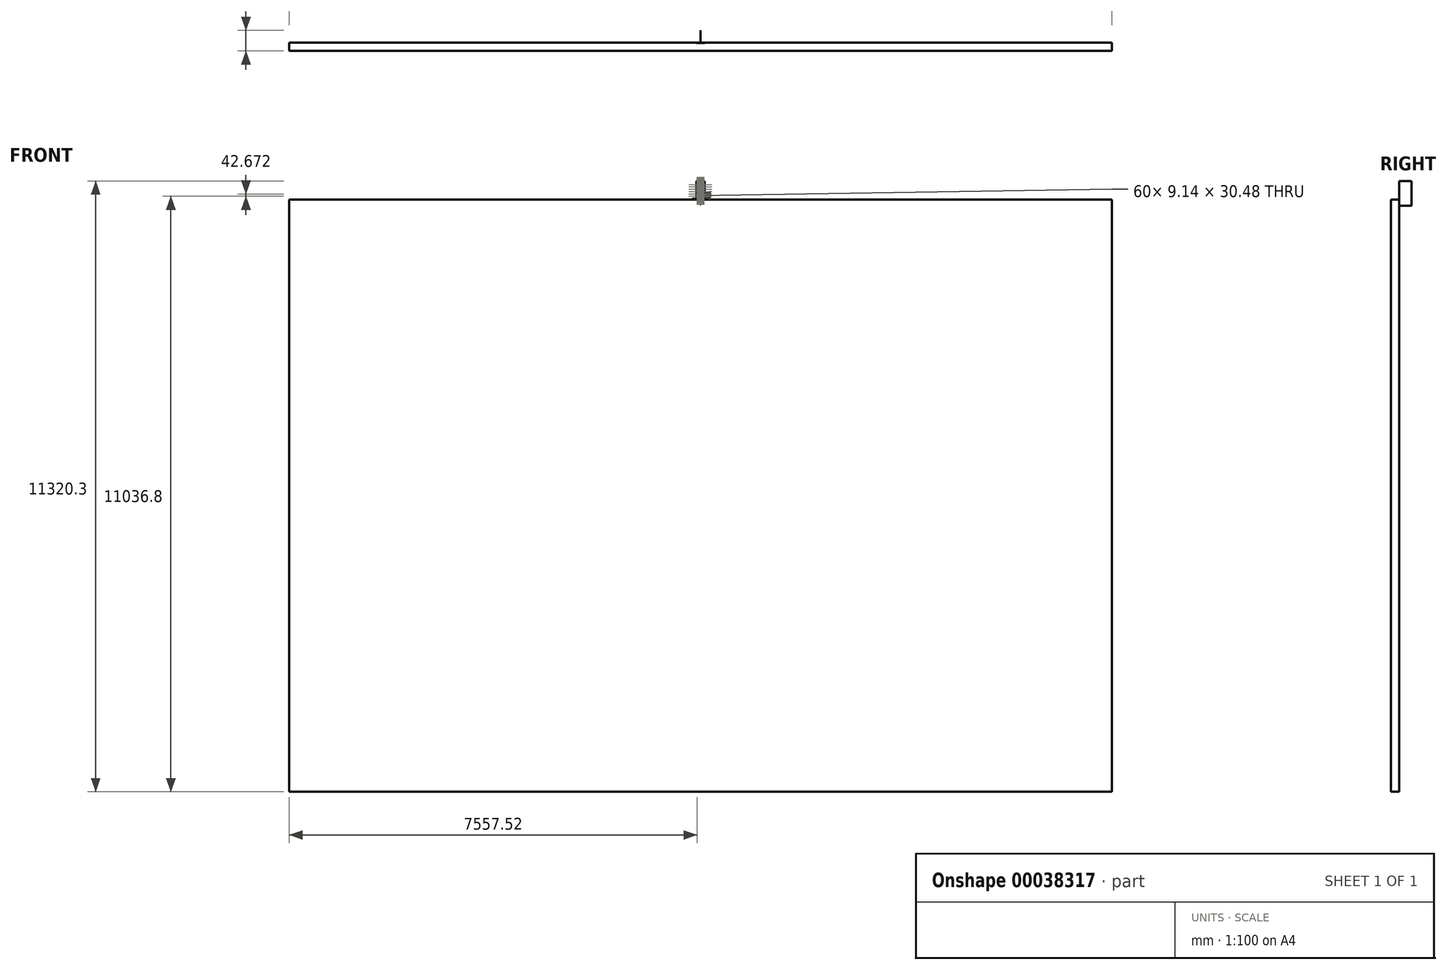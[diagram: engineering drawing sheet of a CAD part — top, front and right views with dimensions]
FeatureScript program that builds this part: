
annotation { "Feature Type Name" : "Feature", "Feature Type Description" : "" }
export const myFeature = defineFeature(function(context is Context, id is Id, definition is map)
    precondition{}
    {
        {
            var Q0;
            Q0=qCreatedBy(makeId("Front.planeOp"),FACE);
            var sketch = newSketch(context, id + "F0", { "sketchPlane" : qUnion([Q0])});
            skLineSegment(sketch, "E0", {"start": v(0, 0) * mm, "end": v(0, 37251.06) * mm, "construction": true});
            skLineSegment(sketch, "E1.bottom", {"start": v(-7620, 0) * mm, "end": v(7620, 0) * mm});
            skLineSegment(sketch, "E1.top", {"start": v(-7620, 34747.2) * mm, "end": v(7620, 34747.2) * mm});
            skLineSegment(sketch, "E1.left", {"start": v(-7620, 0) * mm, "end": v(-7620, 34747.2) * mm});
            skLineSegment(sketch, "E1.right", {"start": v(7620, 0) * mm, "end": v(7620, 34747.2) * mm});
            skLineSegment(sketch, "E2.bottom", {"start": v(-6705.6, 4876.8) * mm, "end": v(-5791.2, 4876.8) * mm});
            skLineSegment(sketch, "E2.top", {"start": v(-6705.6, 7924.8) * mm, "end": v(-5791.2, 7924.8) * mm});
            skLineSegment(sketch, "E2.left", {"start": v(-6705.6, 4876.8) * mm, "end": v(-6705.6, 7924.8) * mm});
            skLineSegment(sketch, "E2.right", {"start": v(-5791.2, 4876.8) * mm, "end": v(-5791.2, 7924.8) * mm});
            skLineSegment(sketch, "E3.0.1.0", {"start": v(-6705.6, 9144) * mm, "end": v(-6705.6, 12192) * mm});
            skLineSegment(sketch, "E3.0.1.1", {"start": v(-5791.2, 9144) * mm, "end": v(-5791.2, 12192) * mm});
            skLineSegment(sketch, "E3.0.1.2", {"start": v(-6705.6, 12192) * mm, "end": v(-5791.2, 12192) * mm});
            skLineSegment(sketch, "E3.0.1.3", {"start": v(-6705.6, 9144) * mm, "end": v(-5791.2, 9144) * mm});
            skLineSegment(sketch, "E3.0.2.0", {"start": v(-6705.6, 13411.2) * mm, "end": v(-6705.6, 16459.2) * mm});
            skLineSegment(sketch, "E3.0.2.1", {"start": v(-5791.2, 13411.2) * mm, "end": v(-5791.2, 16459.2) * mm});
            skLineSegment(sketch, "E3.0.2.2", {"start": v(-6705.6, 16459.2) * mm, "end": v(-5791.2, 16459.2) * mm});
            skLineSegment(sketch, "E3.0.2.3", {"start": v(-6705.6, 13411.2) * mm, "end": v(-5791.2, 13411.2) * mm});
            skLineSegment(sketch, "E3.0.3.0", {"start": v(-6705.6, 17678.4) * mm, "end": v(-6705.6, 20726.4) * mm});
            skLineSegment(sketch, "E3.0.3.1", {"start": v(-5791.2, 17678.4) * mm, "end": v(-5791.2, 20726.4) * mm});
            skLineSegment(sketch, "E3.0.3.2", {"start": v(-6705.6, 20726.4) * mm, "end": v(-5791.2, 20726.4) * mm});
            skLineSegment(sketch, "E3.0.3.3", {"start": v(-6705.6, 17678.4) * mm, "end": v(-5791.2, 17678.4) * mm});
            skLineSegment(sketch, "E3.0.4.0", {"start": v(-6705.6, 21945.6) * mm, "end": v(-6705.6, 24993.6) * mm});
            skLineSegment(sketch, "E3.0.4.1", {"start": v(-5791.2, 21945.6) * mm, "end": v(-5791.2, 24993.6) * mm});
            skLineSegment(sketch, "E3.0.4.2", {"start": v(-6705.6, 24993.6) * mm, "end": v(-5791.2, 24993.6) * mm});
            skLineSegment(sketch, "E3.0.4.3", {"start": v(-6705.6, 21945.6) * mm, "end": v(-5791.2, 21945.6) * mm});
            skLineSegment(sketch, "E3.0.5.0", {"start": v(-6705.6, 26212.8) * mm, "end": v(-6705.6, 29260.8) * mm});
            skLineSegment(sketch, "E3.0.5.1", {"start": v(-5791.2, 26212.8) * mm, "end": v(-5791.2, 29260.8) * mm});
            skLineSegment(sketch, "E3.0.5.2", {"start": v(-6705.6, 29260.8) * mm, "end": v(-5791.2, 29260.8) * mm});
            skLineSegment(sketch, "E3.0.5.3", {"start": v(-6705.6, 26212.8) * mm, "end": v(-5791.2, 26212.8) * mm});
            skLineSegment(sketch, "E3.1.0.0", {"start": v(-5486.4, 4876.8) * mm, "end": v(-5486.4, 7924.8) * mm});
            skLineSegment(sketch, "E3.1.0.1", {"start": v(-4572, 4876.8) * mm, "end": v(-4572, 7924.8) * mm});
            skLineSegment(sketch, "E3.1.0.2", {"start": v(-5486.4, 7924.8) * mm, "end": v(-4572, 7924.8) * mm});
            skLineSegment(sketch, "E3.1.0.3", {"start": v(-5486.4, 4876.8) * mm, "end": v(-4572, 4876.8) * mm});
            skLineSegment(sketch, "E3.1.1.0", {"start": v(-5486.4, 9144) * mm, "end": v(-5486.4, 12192) * mm});
            skLineSegment(sketch, "E3.1.1.1", {"start": v(-4572, 9144) * mm, "end": v(-4572, 12192) * mm});
            skLineSegment(sketch, "E3.1.1.2", {"start": v(-5486.4, 12192) * mm, "end": v(-4572, 12192) * mm});
            skLineSegment(sketch, "E3.1.1.3", {"start": v(-5486.4, 9144) * mm, "end": v(-4572, 9144) * mm});
            skLineSegment(sketch, "E3.1.2.0", {"start": v(-5486.4, 13411.2) * mm, "end": v(-5486.4, 16459.2) * mm});
            skLineSegment(sketch, "E3.1.2.1", {"start": v(-4572, 13411.2) * mm, "end": v(-4572, 16459.2) * mm});
            skLineSegment(sketch, "E3.1.2.2", {"start": v(-5486.4, 16459.2) * mm, "end": v(-4572, 16459.2) * mm});
            skLineSegment(sketch, "E3.1.2.3", {"start": v(-5486.4, 13411.2) * mm, "end": v(-4572, 13411.2) * mm});
            skLineSegment(sketch, "E3.1.3.0", {"start": v(-5486.4, 17678.4) * mm, "end": v(-5486.4, 20726.4) * mm});
            skLineSegment(sketch, "E3.1.3.1", {"start": v(-4572, 17678.4) * mm, "end": v(-4572, 20726.4) * mm});
            skLineSegment(sketch, "E3.1.3.2", {"start": v(-5486.4, 20726.4) * mm, "end": v(-4572, 20726.4) * mm});
            skLineSegment(sketch, "E3.1.3.3", {"start": v(-5486.4, 17678.4) * mm, "end": v(-4572, 17678.4) * mm});
            skLineSegment(sketch, "E3.1.4.0", {"start": v(-5486.4, 21945.6) * mm, "end": v(-5486.4, 24993.6) * mm});
            skLineSegment(sketch, "E3.1.4.1", {"start": v(-4572, 21945.6) * mm, "end": v(-4572, 24993.6) * mm});
            skLineSegment(sketch, "E3.1.4.2", {"start": v(-5486.4, 24993.6) * mm, "end": v(-4572, 24993.6) * mm});
            skLineSegment(sketch, "E3.1.4.3", {"start": v(-5486.4, 21945.6) * mm, "end": v(-4572, 21945.6) * mm});
            skLineSegment(sketch, "E3.1.5.0", {"start": v(-5486.4, 26212.8) * mm, "end": v(-5486.4, 29260.8) * mm});
            skLineSegment(sketch, "E3.1.5.1", {"start": v(-4572, 26212.8) * mm, "end": v(-4572, 29260.8) * mm});
            skLineSegment(sketch, "E3.1.5.2", {"start": v(-5486.4, 29260.8) * mm, "end": v(-4572, 29260.8) * mm});
            skLineSegment(sketch, "E3.1.5.3", {"start": v(-5486.4, 26212.8) * mm, "end": v(-4572, 26212.8) * mm});
            skLineSegment(sketch, "E3.2.0.0", {"start": v(-4267.2, 4876.8) * mm, "end": v(-4267.2, 7924.8) * mm});
            skLineSegment(sketch, "E3.2.0.1", {"start": v(-3352.8, 4876.8) * mm, "end": v(-3352.8, 7924.8) * mm});
            skLineSegment(sketch, "E3.2.0.2", {"start": v(-4267.2, 7924.8) * mm, "end": v(-3352.8, 7924.8) * mm});
            skLineSegment(sketch, "E3.2.0.3", {"start": v(-4267.2, 4876.8) * mm, "end": v(-3352.8, 4876.8) * mm});
            skLineSegment(sketch, "E3.2.1.0", {"start": v(-4267.2, 9144) * mm, "end": v(-4267.2, 12192) * mm});
            skLineSegment(sketch, "E3.2.1.1", {"start": v(-3352.8, 9144) * mm, "end": v(-3352.8, 12192) * mm});
            skLineSegment(sketch, "E3.2.1.2", {"start": v(-4267.2, 12192) * mm, "end": v(-3352.8, 12192) * mm});
            skLineSegment(sketch, "E3.2.1.3", {"start": v(-4267.2, 9144) * mm, "end": v(-3352.8, 9144) * mm});
            skLineSegment(sketch, "E3.2.2.0", {"start": v(-4267.2, 13411.2) * mm, "end": v(-4267.2, 16459.2) * mm});
            skLineSegment(sketch, "E3.2.2.1", {"start": v(-3352.8, 13411.2) * mm, "end": v(-3352.8, 16459.2) * mm});
            skLineSegment(sketch, "E3.2.2.2", {"start": v(-4267.2, 16459.2) * mm, "end": v(-3352.8, 16459.2) * mm});
            skLineSegment(sketch, "E3.2.2.3", {"start": v(-4267.2, 13411.2) * mm, "end": v(-3352.8, 13411.2) * mm});
            skLineSegment(sketch, "E3.2.3.0", {"start": v(-4267.2, 17678.4) * mm, "end": v(-4267.2, 20726.4) * mm});
            skLineSegment(sketch, "E3.2.3.1", {"start": v(-3352.8, 17678.4) * mm, "end": v(-3352.8, 20726.4) * mm});
            skLineSegment(sketch, "E3.2.3.2", {"start": v(-4267.2, 20726.4) * mm, "end": v(-3352.8, 20726.4) * mm});
            skLineSegment(sketch, "E3.2.3.3", {"start": v(-4267.2, 17678.4) * mm, "end": v(-3352.8, 17678.4) * mm});
            skLineSegment(sketch, "E3.2.4.0", {"start": v(-4267.2, 21945.6) * mm, "end": v(-4267.2, 24993.6) * mm});
            skLineSegment(sketch, "E3.2.4.1", {"start": v(-3352.8, 21945.6) * mm, "end": v(-3352.8, 24993.6) * mm});
            skLineSegment(sketch, "E3.2.4.2", {"start": v(-4267.2, 24993.6) * mm, "end": v(-3352.8, 24993.6) * mm});
            skLineSegment(sketch, "E3.2.4.3", {"start": v(-4267.2, 21945.6) * mm, "end": v(-3352.8, 21945.6) * mm});
            skLineSegment(sketch, "E3.2.5.0", {"start": v(-4267.2, 26212.8) * mm, "end": v(-4267.2, 29260.8) * mm});
            skLineSegment(sketch, "E3.2.5.1", {"start": v(-3352.8, 26212.8) * mm, "end": v(-3352.8, 29260.8) * mm});
            skLineSegment(sketch, "E3.2.5.2", {"start": v(-4267.2, 29260.8) * mm, "end": v(-3352.8, 29260.8) * mm});
            skLineSegment(sketch, "E3.2.5.3", {"start": v(-4267.2, 26212.8) * mm, "end": v(-3352.8, 26212.8) * mm});
            skLineSegment(sketch, "E3.direction1", {"start": v(-6705.6, 4876.8) * mm, "end": v(-5486.4, 4876.8) * mm, "construction": true});
            skLineSegment(sketch, "E3.direction2", {"start": v(-6705.6, 4876.8) * mm, "end": v(-6705.6, 9144) * mm, "construction": true});
            skLineSegment(sketch, "E4.MirrorCS", {"start": v(5486.4, 9144) * mm, "end": v(4572, 9144) * mm});
            skLineSegment(sketch, "E5.MirrorCS", {"start": v(5486.4, 7924.8) * mm, "end": v(4572, 7924.8) * mm});
            skLineSegment(sketch, "E6.MirrorCS", {"start": v(6705.6, 4876.8) * mm, "end": v(5791.2, 4876.8) * mm});
            skLineSegment(sketch, "E7.MirrorCS", {"start": v(6705.6, 7924.8) * mm, "end": v(5791.2, 7924.8) * mm});
            skLineSegment(sketch, "E8.MirrorCS", {"start": v(6705.6, 9144) * mm, "end": v(5791.2, 9144) * mm});
            skLineSegment(sketch, "E9.MirrorCS", {"start": v(4267.2, 20726.4) * mm, "end": v(3352.8, 20726.4) * mm});
            skLineSegment(sketch, "E10.MirrorCS", {"start": v(5486.4, 29260.8) * mm, "end": v(4572, 29260.8) * mm});
            skLineSegment(sketch, "E11.MirrorCS", {"start": v(5486.4, 12192) * mm, "end": v(4572, 12192) * mm});
            skLineSegment(sketch, "E12.MirrorCS", {"start": v(4267.2, 12192) * mm, "end": v(3352.8, 12192) * mm});
            skLineSegment(sketch, "E13.MirrorCS", {"start": v(5486.4, 20726.4) * mm, "end": v(4572, 20726.4) * mm});
            skLineSegment(sketch, "E14.MirrorCS", {"start": v(4267.2, 29260.8) * mm, "end": v(3352.8, 29260.8) * mm});
            skLineSegment(sketch, "E15.MirrorCS", {"start": v(6705.6, 17678.4) * mm, "end": v(5791.2, 17678.4) * mm});
            skLineSegment(sketch, "E16.MirrorCS", {"start": v(4267.2, 17678.4) * mm, "end": v(3352.8, 17678.4) * mm});
            skLineSegment(sketch, "E17.MirrorCS", {"start": v(5486.4, 26212.8) * mm, "end": v(4572, 26212.8) * mm});
            skLineSegment(sketch, "E18.MirrorCS", {"start": v(4267.2, 9144) * mm, "end": v(3352.8, 9144) * mm});
            skLineSegment(sketch, "E19.MirrorCS", {"start": v(5486.4, 17678.4) * mm, "end": v(4572, 17678.4) * mm});
            skLineSegment(sketch, "E20.MirrorCS", {"start": v(6705.6, 26212.8) * mm, "end": v(5791.2, 26212.8) * mm});
            skLineSegment(sketch, "E21.MirrorCS", {"start": v(4267.2, 26212.8) * mm, "end": v(3352.8, 26212.8) * mm});
            skLineSegment(sketch, "E22.MirrorCS", {"start": v(4267.2, 16459.2) * mm, "end": v(3352.8, 16459.2) * mm});
            skLineSegment(sketch, "E23.MirrorCS", {"start": v(5486.4, 24993.6) * mm, "end": v(4572, 24993.6) * mm});
            skLineSegment(sketch, "E24.MirrorCS", {"start": v(6705.6, 16459.2) * mm, "end": v(5791.2, 16459.2) * mm});
            skLineSegment(sketch, "E25.MirrorCS", {"start": v(4267.2, 7924.8) * mm, "end": v(3352.8, 7924.8) * mm});
            skLineSegment(sketch, "E26.MirrorCS", {"start": v(5486.4, 16459.2) * mm, "end": v(4572, 16459.2) * mm});
            skLineSegment(sketch, "E27.MirrorCS", {"start": v(6705.6, 24993.6) * mm, "end": v(5791.2, 24993.6) * mm});
            skLineSegment(sketch, "E28.MirrorCS", {"start": v(4267.2, 24993.6) * mm, "end": v(3352.8, 24993.6) * mm});
            skLineSegment(sketch, "E29.MirrorCS", {"start": v(4267.2, 13411.2) * mm, "end": v(3352.8, 13411.2) * mm});
            skLineSegment(sketch, "E30.MirrorCS", {"start": v(5486.4, 21945.6) * mm, "end": v(4572, 21945.6) * mm});
            skLineSegment(sketch, "E31.MirrorCS", {"start": v(5486.4, 4876.8) * mm, "end": v(4572, 4876.8) * mm});
            skLineSegment(sketch, "E32.MirrorCS", {"start": v(4267.2, 4876.8) * mm, "end": v(3352.8, 4876.8) * mm});
            skLineSegment(sketch, "E33.MirrorCS", {"start": v(5486.4, 13411.2) * mm, "end": v(4572, 13411.2) * mm});
            skLineSegment(sketch, "E34.MirrorCS", {"start": v(4267.2, 21945.6) * mm, "end": v(3352.8, 21945.6) * mm});
            skLineSegment(sketch, "E35.MirrorCS", {"start": v(6705.6, 20726.4) * mm, "end": v(5791.2, 20726.4) * mm});
            skLineSegment(sketch, "E36.MirrorCS", {"start": v(6705.6, 29260.8) * mm, "end": v(5791.2, 29260.8) * mm});
            skLineSegment(sketch, "E37.MirrorCS", {"start": v(6705.6, 12192) * mm, "end": v(5791.2, 12192) * mm});
            skLineSegment(sketch, "E38.MirrorCS", {"start": v(6705.6, 13411.2) * mm, "end": v(5791.2, 13411.2) * mm});
            skLineSegment(sketch, "E39.MirrorCS", {"start": v(6705.6, 21945.6) * mm, "end": v(5791.2, 21945.6) * mm});
            skLineSegment(sketch, "E40.MirrorCS", {"start": v(3352.8, 9144) * mm, "end": v(3352.8, 12192) * mm});
            skLineSegment(sketch, "E41.MirrorCS", {"start": v(4572, 17678.4) * mm, "end": v(4572, 20726.4) * mm});
            skLineSegment(sketch, "E42.MirrorCS", {"start": v(3352.8, 26212.8) * mm, "end": v(3352.8, 29260.8) * mm});
            skLineSegment(sketch, "E43.MirrorCS", {"start": v(5791.2, 26212.8) * mm, "end": v(5791.2, 29260.8) * mm});
            skLineSegment(sketch, "E44.MirrorCS", {"start": v(4267.2, 13411.2) * mm, "end": v(4267.2, 16459.2) * mm});
            skLineSegment(sketch, "E45.MirrorCS", {"start": v(5486.4, 21945.6) * mm, "end": v(5486.4, 24993.6) * mm});
            skLineSegment(sketch, "E46.MirrorCS", {"start": v(5486.4, 4876.8) * mm, "end": v(5486.4, 7924.8) * mm});
            skLineSegment(sketch, "E47.MirrorCS", {"start": v(6705.6, 21945.6) * mm, "end": v(6705.6, 24993.6) * mm});
            skLineSegment(sketch, "E48.MirrorCS", {"start": v(3352.8, 13411.2) * mm, "end": v(3352.8, 16459.2) * mm});
            skLineSegment(sketch, "E49.MirrorCS", {"start": v(4267.2, 21945.6) * mm, "end": v(4267.2, 24993.6) * mm});
            skLineSegment(sketch, "E50.MirrorCS", {"start": v(4267.2, 4876.8) * mm, "end": v(4267.2, 7924.8) * mm});
            skLineSegment(sketch, "E51.MirrorCS", {"start": v(4572, 21945.6) * mm, "end": v(4572, 24993.6) * mm});
            skLineSegment(sketch, "E52.MirrorCS", {"start": v(5486.4, 13411.2) * mm, "end": v(5486.4, 16459.2) * mm});
            skLineSegment(sketch, "E53.MirrorCS", {"start": v(4572, 4876.8) * mm, "end": v(4572, 7924.8) * mm});
            skLineSegment(sketch, "E54.MirrorCS", {"start": v(5791.2, 21945.6) * mm, "end": v(5791.2, 24993.6) * mm});
            skLineSegment(sketch, "E55.MirrorCS", {"start": v(3352.8, 21945.6) * mm, "end": v(3352.8, 24993.6) * mm});
            skLineSegment(sketch, "E56.MirrorCS", {"start": v(3352.8, 4876.8) * mm, "end": v(3352.8, 7924.8) * mm});
            skLineSegment(sketch, "E57.MirrorCS", {"start": v(4572, 13411.2) * mm, "end": v(4572, 16459.2) * mm});
            skLineSegment(sketch, "E58.MirrorCS", {"start": v(6705.6, 13411.2) * mm, "end": v(6705.6, 16459.2) * mm});
            skLineSegment(sketch, "E59.MirrorCS", {"start": v(5791.2, 13411.2) * mm, "end": v(5791.2, 16459.2) * mm});
            skLineSegment(sketch, "E60.MirrorCS", {"start": v(6705.6, 4876.8) * mm, "end": v(6705.6, 7924.8) * mm});
            skLineSegment(sketch, "E61.MirrorCS", {"start": v(5791.2, 4876.8) * mm, "end": v(5791.2, 7924.8) * mm});
            skLineSegment(sketch, "E62.MirrorCS", {"start": v(6705.6, 9144) * mm, "end": v(6705.6, 12192) * mm});
            skLineSegment(sketch, "E63.MirrorCS", {"start": v(5791.2, 9144) * mm, "end": v(5791.2, 12192) * mm});
            skLineSegment(sketch, "E64.MirrorCS", {"start": v(6705.6, 17678.4) * mm, "end": v(6705.6, 20726.4) * mm});
            skLineSegment(sketch, "E65.MirrorCS", {"start": v(4267.2, 17678.4) * mm, "end": v(4267.2, 20726.4) * mm});
            skLineSegment(sketch, "E66.MirrorCS", {"start": v(5486.4, 26212.8) * mm, "end": v(5486.4, 29260.8) * mm});
            skLineSegment(sketch, "E67.MirrorCS", {"start": v(5486.4, 9144) * mm, "end": v(5486.4, 12192) * mm});
            skLineSegment(sketch, "E68.MirrorCS", {"start": v(4267.2, 9144) * mm, "end": v(4267.2, 12192) * mm});
            skLineSegment(sketch, "E69.MirrorCS", {"start": v(5486.4, 17678.4) * mm, "end": v(5486.4, 20726.4) * mm});
            skLineSegment(sketch, "E70.MirrorCS", {"start": v(4267.2, 26212.8) * mm, "end": v(4267.2, 29260.8) * mm});
            skLineSegment(sketch, "E71.MirrorCS", {"start": v(6705.6, 26212.8) * mm, "end": v(6705.6, 29260.8) * mm});
            skLineSegment(sketch, "E72.MirrorCS", {"start": v(4572, 9144) * mm, "end": v(4572, 12192) * mm});
            skLineSegment(sketch, "E73.MirrorCS", {"start": v(4572, 26212.8) * mm, "end": v(4572, 29260.8) * mm});
            skLineSegment(sketch, "E74.MirrorCS", {"start": v(3352.8, 17678.4) * mm, "end": v(3352.8, 20726.4) * mm});
            skLineSegment(sketch, "E75.MirrorCS", {"start": v(5791.2, 17678.4) * mm, "end": v(5791.2, 20726.4) * mm});
            skLineSegment(sketch, "E76.bottom", {"start": v(6705.6, 31089.6) * mm, "end": v(5791.2, 31089.6) * mm});
            skLineSegment(sketch, "E76.top", {"start": v(6705.6, 32918.4) * mm, "end": v(5791.2, 32918.4) * mm});
            skLineSegment(sketch, "E76.left", {"start": v(6705.6, 31089.6) * mm, "end": v(6705.6, 32918.4) * mm});
            skLineSegment(sketch, "E76.right", {"start": v(5791.2, 31089.6) * mm, "end": v(5791.2, 32918.4) * mm});
            skLineSegment(sketch, "E77.bottom", {"start": v(5486.4, 31089.6) * mm, "end": v(4572, 31089.6) * mm});
            skLineSegment(sketch, "E77.top", {"start": v(5486.4, 32918.4) * mm, "end": v(4572, 32918.4) * mm});
            skLineSegment(sketch, "E77.left", {"start": v(5486.4, 31089.6) * mm, "end": v(5486.4, 32918.4) * mm});
            skLineSegment(sketch, "E77.right", {"start": v(4572, 31089.6) * mm, "end": v(4572, 32918.4) * mm});
            skLineSegment(sketch, "E78.bottom", {"start": v(4267.2, 31089.6) * mm, "end": v(3352.8, 31089.6) * mm});
            skLineSegment(sketch, "E78.top", {"start": v(4267.2, 32918.4) * mm, "end": v(3352.8, 32918.4) * mm});
            skLineSegment(sketch, "E78.left", {"start": v(4267.2, 31089.6) * mm, "end": v(4267.2, 32918.4) * mm});
            skLineSegment(sketch, "E78.right", {"start": v(3352.8, 31089.6) * mm, "end": v(3352.8, 32918.4) * mm});
            skLineSegment(sketch, "E79.bottom", {"start": v(-6705.6, 31089.6) * mm, "end": v(-5791.2, 31089.6) * mm});
            skLineSegment(sketch, "E79.top", {"start": v(-6705.6, 32918.4) * mm, "end": v(-5791.2, 32918.4) * mm});
            skLineSegment(sketch, "E79.left", {"start": v(-6705.6, 31089.6) * mm, "end": v(-6705.6, 32918.4) * mm});
            skLineSegment(sketch, "E79.right", {"start": v(-5791.2, 31089.6) * mm, "end": v(-5791.2, 32918.4) * mm});
            skLineSegment(sketch, "E80.bottom", {"start": v(-5486.4, 31089.6) * mm, "end": v(-4572, 31089.6) * mm});
            skLineSegment(sketch, "E80.top", {"start": v(-5486.4, 32918.4) * mm, "end": v(-4572, 32918.4) * mm});
            skLineSegment(sketch, "E80.left", {"start": v(-5486.4, 31089.6) * mm, "end": v(-5486.4, 32918.4) * mm});
            skLineSegment(sketch, "E80.right", {"start": v(-4572, 31089.6) * mm, "end": v(-4572, 32918.4) * mm});
            skLineSegment(sketch, "E81.bottom", {"start": v(-4267.2, 31089.6) * mm, "end": v(-3352.8, 31089.6) * mm});
            skLineSegment(sketch, "E81.top", {"start": v(-4267.2, 32918.4) * mm, "end": v(-3352.8, 32918.4) * mm});
            skLineSegment(sketch, "E81.left", {"start": v(-4267.2, 31089.6) * mm, "end": v(-4267.2, 32918.4) * mm});
            skLineSegment(sketch, "E81.right", {"start": v(-3352.8, 31089.6) * mm, "end": v(-3352.8, 32918.4) * mm});
            skLineSegment(sketch, "E82.bottom", {"start": v(-2286, 4876.8) * mm, "end": v(-1371.6, 4876.8) * mm});
            skLineSegment(sketch, "E82.top", {"start": v(-2286, 7924.8) * mm, "end": v(-1371.6, 7924.8) * mm});
            skLineSegment(sketch, "E82.left", {"start": v(-2286, 4876.8) * mm, "end": v(-2286, 7924.8) * mm});
            skLineSegment(sketch, "E82.right", {"start": v(-1371.6, 4876.8) * mm, "end": v(-1371.6, 7924.8) * mm});
            skLineSegment(sketch, "E83.0.1.0", {"start": v(-2286, 12192) * mm, "end": v(-1371.6, 12192) * mm});
            skLineSegment(sketch, "E83.0.1.1", {"start": v(-1371.6, 9144) * mm, "end": v(-1371.6, 12192) * mm});
            skLineSegment(sketch, "E83.0.1.2", {"start": v(-2286, 9144) * mm, "end": v(-1371.6, 9144) * mm});
            skLineSegment(sketch, "E83.0.1.3", {"start": v(-2286, 9144) * mm, "end": v(-2286, 12192) * mm});
            skLineSegment(sketch, "E83.0.2.0", {"start": v(-2286, 16459.2) * mm, "end": v(-1371.6, 16459.2) * mm});
            skLineSegment(sketch, "E83.0.2.1", {"start": v(-1371.6, 13411.2) * mm, "end": v(-1371.6, 16459.2) * mm});
            skLineSegment(sketch, "E83.0.2.2", {"start": v(-2286, 13411.2) * mm, "end": v(-1371.6, 13411.2) * mm});
            skLineSegment(sketch, "E83.0.2.3", {"start": v(-2286, 13411.2) * mm, "end": v(-2286, 16459.2) * mm});
            skLineSegment(sketch, "E83.0.3.0", {"start": v(-2286, 20726.4) * mm, "end": v(-1371.6, 20726.4) * mm});
            skLineSegment(sketch, "E83.0.3.1", {"start": v(-1371.6, 17678.4) * mm, "end": v(-1371.6, 20726.4) * mm});
            skLineSegment(sketch, "E83.0.3.2", {"start": v(-2286, 17678.4) * mm, "end": v(-1371.6, 17678.4) * mm});
            skLineSegment(sketch, "E83.0.3.3", {"start": v(-2286, 17678.4) * mm, "end": v(-2286, 20726.4) * mm});
            skLineSegment(sketch, "E83.0.4.0", {"start": v(-2286, 24993.6) * mm, "end": v(-1371.6, 24993.6) * mm});
            skLineSegment(sketch, "E83.0.4.1", {"start": v(-1371.6, 21945.6) * mm, "end": v(-1371.6, 24993.6) * mm});
            skLineSegment(sketch, "E83.0.4.2", {"start": v(-2286, 21945.6) * mm, "end": v(-1371.6, 21945.6) * mm});
            skLineSegment(sketch, "E83.0.4.3", {"start": v(-2286, 21945.6) * mm, "end": v(-2286, 24993.6) * mm});
            skLineSegment(sketch, "E83.0.5.0", {"start": v(-2286, 29260.8) * mm, "end": v(-1371.6, 29260.8) * mm});
            skLineSegment(sketch, "E83.0.5.1", {"start": v(-1371.6, 26212.8) * mm, "end": v(-1371.6, 29260.8) * mm});
            skLineSegment(sketch, "E83.0.5.2", {"start": v(-2286, 26212.8) * mm, "end": v(-1371.6, 26212.8) * mm});
            skLineSegment(sketch, "E83.0.5.3", {"start": v(-2286, 26212.8) * mm, "end": v(-2286, 29260.8) * mm});
            skLineSegment(sketch, "E83.1.0.0", {"start": v(-1066.8, 7924.8) * mm, "end": v(-152.4, 7924.8) * mm});
            skLineSegment(sketch, "E83.1.0.1", {"start": v(-152.4, 4876.8) * mm, "end": v(-152.4, 7924.8) * mm});
            skLineSegment(sketch, "E83.1.0.2", {"start": v(-1066.8, 4876.8) * mm, "end": v(-152.4, 4876.8) * mm});
            skLineSegment(sketch, "E83.1.0.3", {"start": v(-1066.8, 4876.8) * mm, "end": v(-1066.8, 7924.8) * mm});
            skLineSegment(sketch, "E83.1.1.0", {"start": v(-1066.8, 12192) * mm, "end": v(-152.4, 12192) * mm});
            skLineSegment(sketch, "E83.1.1.1", {"start": v(-152.4, 9144) * mm, "end": v(-152.4, 12192) * mm});
            skLineSegment(sketch, "E83.1.1.2", {"start": v(-1066.8, 9144) * mm, "end": v(-152.4, 9144) * mm});
            skLineSegment(sketch, "E83.1.1.3", {"start": v(-1066.8, 9144) * mm, "end": v(-1066.8, 12192) * mm});
            skLineSegment(sketch, "E83.1.2.0", {"start": v(-1066.8, 16459.2) * mm, "end": v(-152.4, 16459.2) * mm});
            skLineSegment(sketch, "E83.1.2.1", {"start": v(-152.4, 13411.2) * mm, "end": v(-152.4, 16459.2) * mm});
            skLineSegment(sketch, "E83.1.2.2", {"start": v(-1066.8, 13411.2) * mm, "end": v(-152.4, 13411.2) * mm});
            skLineSegment(sketch, "E83.1.2.3", {"start": v(-1066.8, 13411.2) * mm, "end": v(-1066.8, 16459.2) * mm});
            skLineSegment(sketch, "E83.1.3.0", {"start": v(-1066.8, 20726.4) * mm, "end": v(-152.4, 20726.4) * mm});
            skLineSegment(sketch, "E83.1.3.1", {"start": v(-152.4, 17678.4) * mm, "end": v(-152.4, 20726.4) * mm});
            skLineSegment(sketch, "E83.1.3.2", {"start": v(-1066.8, 17678.4) * mm, "end": v(-152.4, 17678.4) * mm});
            skLineSegment(sketch, "E83.1.3.3", {"start": v(-1066.8, 17678.4) * mm, "end": v(-1066.8, 20726.4) * mm});
            skLineSegment(sketch, "E83.1.4.0", {"start": v(-1066.8, 24993.6) * mm, "end": v(-152.4, 24993.6) * mm});
            skLineSegment(sketch, "E83.1.4.1", {"start": v(-152.4, 21945.6) * mm, "end": v(-152.4, 24993.6) * mm});
            skLineSegment(sketch, "E83.1.4.2", {"start": v(-1066.8, 21945.6) * mm, "end": v(-152.4, 21945.6) * mm});
            skLineSegment(sketch, "E83.1.4.3", {"start": v(-1066.8, 21945.6) * mm, "end": v(-1066.8, 24993.6) * mm});
            skLineSegment(sketch, "E83.1.5.0", {"start": v(-1066.8, 29260.8) * mm, "end": v(-152.4, 29260.8) * mm});
            skLineSegment(sketch, "E83.1.5.1", {"start": v(-152.4, 26212.8) * mm, "end": v(-152.4, 29260.8) * mm});
            skLineSegment(sketch, "E83.1.5.2", {"start": v(-1066.8, 26212.8) * mm, "end": v(-152.4, 26212.8) * mm});
            skLineSegment(sketch, "E83.1.5.3", {"start": v(-1066.8, 26212.8) * mm, "end": v(-1066.8, 29260.8) * mm});
            skLineSegment(sketch, "E83.2.0.0", {"start": v(152.4, 7924.8) * mm, "end": v(1066.8, 7924.8) * mm});
            skLineSegment(sketch, "E83.2.0.1", {"start": v(1066.8, 4876.8) * mm, "end": v(1066.8, 7924.8) * mm});
            skLineSegment(sketch, "E83.2.0.2", {"start": v(152.4, 4876.8) * mm, "end": v(1066.8, 4876.8) * mm});
            skLineSegment(sketch, "E83.2.0.3", {"start": v(152.4, 4876.8) * mm, "end": v(152.4, 7924.8) * mm});
            skLineSegment(sketch, "E83.2.1.0", {"start": v(152.4, 12192) * mm, "end": v(1066.8, 12192) * mm});
            skLineSegment(sketch, "E83.2.1.1", {"start": v(1066.8, 9144) * mm, "end": v(1066.8, 12192) * mm});
            skLineSegment(sketch, "E83.2.1.2", {"start": v(152.4, 9144) * mm, "end": v(1066.8, 9144) * mm});
            skLineSegment(sketch, "E83.2.1.3", {"start": v(152.4, 9144) * mm, "end": v(152.4, 12192) * mm});
            skLineSegment(sketch, "E83.2.2.0", {"start": v(152.4, 16459.2) * mm, "end": v(1066.8, 16459.2) * mm});
            skLineSegment(sketch, "E83.2.2.1", {"start": v(1066.8, 13411.2) * mm, "end": v(1066.8, 16459.2) * mm});
            skLineSegment(sketch, "E83.2.2.2", {"start": v(152.4, 13411.2) * mm, "end": v(1066.8, 13411.2) * mm});
            skLineSegment(sketch, "E83.2.2.3", {"start": v(152.4, 13411.2) * mm, "end": v(152.4, 16459.2) * mm});
            skLineSegment(sketch, "E83.2.3.0", {"start": v(152.4, 20726.4) * mm, "end": v(1066.8, 20726.4) * mm});
            skLineSegment(sketch, "E83.2.3.1", {"start": v(1066.8, 17678.4) * mm, "end": v(1066.8, 20726.4) * mm});
            skLineSegment(sketch, "E83.2.3.2", {"start": v(152.4, 17678.4) * mm, "end": v(1066.8, 17678.4) * mm});
            skLineSegment(sketch, "E83.2.3.3", {"start": v(152.4, 17678.4) * mm, "end": v(152.4, 20726.4) * mm});
            skLineSegment(sketch, "E83.2.4.0", {"start": v(152.4, 24993.6) * mm, "end": v(1066.8, 24993.6) * mm});
            skLineSegment(sketch, "E83.2.4.1", {"start": v(1066.8, 21945.6) * mm, "end": v(1066.8, 24993.6) * mm});
            skLineSegment(sketch, "E83.2.4.2", {"start": v(152.4, 21945.6) * mm, "end": v(1066.8, 21945.6) * mm});
            skLineSegment(sketch, "E83.2.4.3", {"start": v(152.4, 21945.6) * mm, "end": v(152.4, 24993.6) * mm});
            skLineSegment(sketch, "E83.2.5.0", {"start": v(152.4, 29260.8) * mm, "end": v(1066.8, 29260.8) * mm});
            skLineSegment(sketch, "E83.2.5.1", {"start": v(1066.8, 26212.8) * mm, "end": v(1066.8, 29260.8) * mm});
            skLineSegment(sketch, "E83.2.5.2", {"start": v(152.4, 26212.8) * mm, "end": v(1066.8, 26212.8) * mm});
            skLineSegment(sketch, "E83.2.5.3", {"start": v(152.4, 26212.8) * mm, "end": v(152.4, 29260.8) * mm});
            skLineSegment(sketch, "E83.3.0.0", {"start": v(1371.6, 7924.8) * mm, "end": v(2286, 7924.8) * mm});
            skLineSegment(sketch, "E83.3.0.1", {"start": v(2286, 4876.8) * mm, "end": v(2286, 7924.8) * mm});
            skLineSegment(sketch, "E83.3.0.2", {"start": v(1371.6, 4876.8) * mm, "end": v(2286, 4876.8) * mm});
            skLineSegment(sketch, "E83.3.0.3", {"start": v(1371.6, 4876.8) * mm, "end": v(1371.6, 7924.8) * mm});
            skLineSegment(sketch, "E83.3.1.0", {"start": v(1371.6, 12192) * mm, "end": v(2286, 12192) * mm});
            skLineSegment(sketch, "E83.3.1.1", {"start": v(2286, 9144) * mm, "end": v(2286, 12192) * mm});
            skLineSegment(sketch, "E83.3.1.2", {"start": v(1371.6, 9144) * mm, "end": v(2286, 9144) * mm});
            skLineSegment(sketch, "E83.3.1.3", {"start": v(1371.6, 9144) * mm, "end": v(1371.6, 12192) * mm});
            skLineSegment(sketch, "E83.3.2.0", {"start": v(1371.6, 16459.2) * mm, "end": v(2286, 16459.2) * mm});
            skLineSegment(sketch, "E83.3.2.1", {"start": v(2286, 13411.2) * mm, "end": v(2286, 16459.2) * mm});
            skLineSegment(sketch, "E83.3.2.2", {"start": v(1371.6, 13411.2) * mm, "end": v(2286, 13411.2) * mm});
            skLineSegment(sketch, "E83.3.2.3", {"start": v(1371.6, 13411.2) * mm, "end": v(1371.6, 16459.2) * mm});
            skLineSegment(sketch, "E83.3.3.0", {"start": v(1371.6, 20726.4) * mm, "end": v(2286, 20726.4) * mm});
            skLineSegment(sketch, "E83.3.3.1", {"start": v(2286, 17678.4) * mm, "end": v(2286, 20726.4) * mm});
            skLineSegment(sketch, "E83.3.3.2", {"start": v(1371.6, 17678.4) * mm, "end": v(2286, 17678.4) * mm});
            skLineSegment(sketch, "E83.3.3.3", {"start": v(1371.6, 17678.4) * mm, "end": v(1371.6, 20726.4) * mm});
            skLineSegment(sketch, "E83.3.4.0", {"start": v(1371.6, 24993.6) * mm, "end": v(2286, 24993.6) * mm});
            skLineSegment(sketch, "E83.3.4.1", {"start": v(2286, 21945.6) * mm, "end": v(2286, 24993.6) * mm});
            skLineSegment(sketch, "E83.3.4.2", {"start": v(1371.6, 21945.6) * mm, "end": v(2286, 21945.6) * mm});
            skLineSegment(sketch, "E83.3.4.3", {"start": v(1371.6, 21945.6) * mm, "end": v(1371.6, 24993.6) * mm});
            skLineSegment(sketch, "E83.3.5.0", {"start": v(1371.6, 29260.8) * mm, "end": v(2286, 29260.8) * mm});
            skLineSegment(sketch, "E83.3.5.1", {"start": v(2286, 26212.8) * mm, "end": v(2286, 29260.8) * mm});
            skLineSegment(sketch, "E83.3.5.2", {"start": v(1371.6, 26212.8) * mm, "end": v(2286, 26212.8) * mm});
            skLineSegment(sketch, "E83.3.5.3", {"start": v(1371.6, 26212.8) * mm, "end": v(1371.6, 29260.8) * mm});
            skLineSegment(sketch, "E83.direction1", {"start": v(-2286, 7924.8) * mm, "end": v(-1066.8, 7924.8) * mm, "construction": true});
            skLineSegment(sketch, "E83.direction2", {"start": v(-2286, 7924.8) * mm, "end": v(-2286, 12192) * mm, "construction": true});
            skLineSegment(sketch, "E84.bottom", {"start": v(-2286, 31089.6) * mm, "end": v(-1371.6, 31089.6) * mm});
            skLineSegment(sketch, "E84.top", {"start": v(-2286, 32918.4) * mm, "end": v(-1371.6, 32918.4) * mm});
            skLineSegment(sketch, "E84.left", {"start": v(-2286, 31089.6) * mm, "end": v(-2286, 32918.4) * mm});
            skLineSegment(sketch, "E84.right", {"start": v(-1371.6, 31089.6) * mm, "end": v(-1371.6, 32918.4) * mm});
            skLineSegment(sketch, "E85.bottom", {"start": v(-1066.8, 31089.6) * mm, "end": v(-152.4, 31089.6) * mm});
            skLineSegment(sketch, "E85.top", {"start": v(-1066.8, 32918.4) * mm, "end": v(-152.4, 32918.4) * mm});
            skLineSegment(sketch, "E85.left", {"start": v(-1066.8, 31089.6) * mm, "end": v(-1066.8, 32918.4) * mm});
            skLineSegment(sketch, "E85.right", {"start": v(-152.4, 31089.6) * mm, "end": v(-152.4, 32918.4) * mm});
            skLineSegment(sketch, "E86.bottom", {"start": v(152.4, 31089.6) * mm, "end": v(1066.8, 31089.6) * mm});
            skLineSegment(sketch, "E86.top", {"start": v(152.4, 32918.4) * mm, "end": v(1066.8, 32918.4) * mm});
            skLineSegment(sketch, "E86.left", {"start": v(152.4, 31089.6) * mm, "end": v(152.4, 32918.4) * mm});
            skLineSegment(sketch, "E86.right", {"start": v(1066.8, 31089.6) * mm, "end": v(1066.8, 32918.4) * mm});
            skLineSegment(sketch, "E87.bottom", {"start": v(1371.6, 31089.6) * mm, "end": v(2286, 31089.6) * mm});
            skLineSegment(sketch, "E87.top", {"start": v(1371.6, 32918.4) * mm, "end": v(2286, 32918.4) * mm});
            skLineSegment(sketch, "E87.left", {"start": v(1371.6, 31089.6) * mm, "end": v(1371.6, 32918.4) * mm});
            skLineSegment(sketch, "E87.right", {"start": v(2286, 31089.6) * mm, "end": v(2286, 32918.4) * mm});
            skLineSegment(sketch, "E88.bottom", {"start": v(-2286, 3657.6) * mm, "end": v(2286, 3657.6) * mm});
            skLineSegment(sketch, "E88.top", {"start": v(-2286, 0) * mm, "end": v(2286, 0) * mm});
            skLineSegment(sketch, "E88.left", {"start": v(-2286, 3657.6) * mm, "end": v(-2286, 0) * mm});
            skLineSegment(sketch, "E88.right", {"start": v(2286, 3657.6) * mm, "end": v(2286, 0) * mm});
            skLineSegment(sketch, "E89.bottom", {"start": v(3200.4, 3657.6) * mm, "end": v(6705.6, 3657.6) * mm});
            skLineSegment(sketch, "E89.top", {"start": v(3200.4, 0) * mm, "end": v(6705.6, 0) * mm});
            skLineSegment(sketch, "E89.left", {"start": v(3200.4, 3657.6) * mm, "end": v(3200.4, 0) * mm});
            skLineSegment(sketch, "E89.right", {"start": v(6705.6, 3657.6) * mm, "end": v(6705.6, 0) * mm});
            skLineSegment(sketch, "E90.MirrorCS", {"start": v(-3200.4, 0) * mm, "end": v(-6705.6, 0) * mm});
            skLineSegment(sketch, "E91.MirrorCS", {"start": v(-3200.4, 3657.6) * mm, "end": v(-6705.6, 3657.6) * mm});
            skLineSegment(sketch, "E92.MirrorCS", {"start": v(-6705.6, 3657.6) * mm, "end": v(-6705.6, 0) * mm});
            skLineSegment(sketch, "E93.MirrorCS", {"start": v(-3200.4, 3657.6) * mm, "end": v(-3200.4, 0) * mm});
            skSolve(sketch);
        }
        {
            var Q0;
            Q0=qCreatedBy(makeId("Front.planeOp"),FACE);
            var sketch = newSketch(context, id + "F1", { "sketchPlane" : qUnion([Q0])});
            skLineSegment(sketch, "E94.bottom", {"start": v(-7620, 0) * mm, "end": v(7620, 0) * mm});
            skLineSegment(sketch, "E94.top", {"start": v(-7620, -10972.8) * mm, "end": v(7620, -10972.8) * mm});
            skLineSegment(sketch, "E94.left", {"start": v(-7620, 0) * mm, "end": v(-7620, -10972.8) * mm});
            skLineSegment(sketch, "E94.right", {"start": v(7620, 0) * mm, "end": v(7620, -10972.8) * mm});
            skSolve(sketch);
        }
        {
            var Q0;
            Q0=makeQuery(id+"F0.imprint","IMPRINT",FACE,{"disambiguationData":[TD([[makeQuery(id+"F0.imprint","IMPRINT",EDGE,{"derivedFrom":sQuery(id+"F0.wireOp",EDGE,"E1.top")}),-1.0]])]});
            var Q1;
            Q1=makeQuery(id+"F1.imprint","IMPRINT",FACE,{"disambiguationData":[TD([[makeQuery(id+"F1.imprint","IMPRINT",EDGE,{"derivedFrom":sQuery(id+"F1.wireOp",EDGE,"E94.bottom")}),-1.0]])]});
            extrude(context, id + "F2", {"entities" : qUnion([Q0, Q1]), "depth" : 152.4 * mm});
        }
        {
            var Q0;
            Q0=qCreatedBy(makeId("Right.planeOp"),FACE);
            var sketch = newSketch(context, id + "F3", { "sketchPlane" : qUnion([Q0])});
            skLineSegment(sketch, "E95.bottom", {"start": v(0, 0) * mm, "end": v(22860, 0) * mm});
            skLineSegment(sketch, "E95.top", {"start": v(0, 34747.2) * mm, "end": v(22860, 34747.2) * mm});
            skLineSegment(sketch, "E95.left", {"start": v(0, 0) * mm, "end": v(0, 34747.2) * mm});
            skLineSegment(sketch, "E95.right", {"start": v(22860, 0) * mm, "end": v(22860, 34747.2) * mm});
            skLineSegment(sketch, "E96.top", {"start": v(0, -10972.8) * mm, "end": v(22860, -10972.8) * mm});
            skLineSegment(sketch, "E96.left", {"start": v(0, 0) * mm, "end": v(0, -10972.8) * mm});
            skLineSegment(sketch, "E96.right", {"start": v(22860, 0) * mm, "end": v(22860, -10972.8) * mm});
            skSolve(sketch);
        }
        {
            var Q0;
            Q0=makeQuery(id+"F3.imprint","IMPRINT",FACE,{"disambiguationData":[TD([[makeQuery(id+"F3.imprint","IMPRINT",EDGE,{"derivedFrom":sQuery(id+"F3.wireOp",EDGE,"E95.top")}),-1.0]])]});
            var Q1;
            Q1=makeQuery(id+"F3.imprint","IMPRINT",FACE,{"disambiguationData":[TD([[makeQuery(id+"F3.imprint","IMPRINT",EDGE,{"derivedFrom":sQuery(id+"F3.wireOp",EDGE,"E95.bottom")}),-1.0]])]});
            extrude(context, id + "F4", {"entities" : qUnion([Q0, Q1]), "depth" : 152.4 * mm});
        }
        {
            var Q0;
            Q0=makeQuery(id+"F0.imprint","IMPRINT",FACE,{"disambiguationData":[TD([[makeQuery(id+"F0.imprint","IMPRINT",EDGE,{"derivedFrom":sQuery(id+"F0.wireOp",EDGE,"E1.top")}),-1.0]])]});
            var Q1;
            Q1=makeQuery(id+"F1.imprint","IMPRINT",FACE,{"disambiguationData":[TD([[makeQuery(id+"F1.imprint","IMPRINT",EDGE,{"derivedFrom":sQuery(id+"F1.wireOp",EDGE,"E94.bottom")}),-1.0]])]});
            var Q2;
            Q2=makeQuery(id+"F0.imprint","IMPRINT",FACE,{"disambiguationData":[TD([[makeQuery(id+"F0.imprint","IMPRINT",EDGE,{"derivedFrom":sQuery(id+"F0.wireOp",EDGE,"E89.bottom")}),-1.0]])]});
            var Q3;
            Q3=makeQuery(id+"F0.imprint","IMPRINT",FACE,{"disambiguationData":[TD([[makeQuery(id+"F0.imprint","IMPRINT",EDGE,{"derivedFrom":sQuery(id+"F0.wireOp",EDGE,"E88.bottom")}),-1.0]])]});
            var Q4;
            Q4=makeQuery(id+"F0.imprint","IMPRINT",FACE,{"disambiguationData":[TD([[makeQuery(id+"F0.imprint","IMPRINT",EDGE,{"derivedFrom":sQuery(id+"F0.wireOp",EDGE,"E90.MirrorCS")}),-1.0]])]});
            var Q5;
            Q5=makeQuery(id+"F0.imprint","IMPRINT",FACE,{"disambiguationData":[TD([[makeQuery(id+"F0.imprint","IMPRINT",EDGE,{"derivedFrom":sQuery(id+"F0.wireOp",EDGE,"E2.bottom")}),1.0]])]});
            var Q6;
            Q6=makeQuery(id+"F0.imprint","IMPRINT",FACE,{"disambiguationData":[TD([[makeQuery(id+"F0.imprint","IMPRINT",EDGE,{"derivedFrom":sQuery(id+"F0.wireOp",EDGE,"E3.1.0.0")}),-1.0]])]});
            var Q7;
            Q7=makeQuery(id+"F0.imprint","IMPRINT",FACE,{"disambiguationData":[TD([[makeQuery(id+"F0.imprint","IMPRINT",EDGE,{"derivedFrom":sQuery(id+"F0.wireOp",EDGE,"E3.2.0.0")}),-1.0]])]});
            var Q8;
            Q8=makeQuery(id+"F0.imprint","IMPRINT",FACE,{"disambiguationData":[TD([[makeQuery(id+"F0.imprint","IMPRINT",EDGE,{"derivedFrom":sQuery(id+"F0.wireOp",EDGE,"E82.bottom")}),1.0]])]});
            var Q9;
            Q9=makeQuery(id+"F0.imprint","IMPRINT",FACE,{"disambiguationData":[TD([[makeQuery(id+"F0.imprint","IMPRINT",EDGE,{"derivedFrom":sQuery(id+"F0.wireOp",EDGE,"E83.1.0.0")}),-1.0]])]});
            var Q10;
            Q10=makeQuery(id+"F0.imprint","IMPRINT",FACE,{"disambiguationData":[TD([[makeQuery(id+"F0.imprint","IMPRINT",EDGE,{"derivedFrom":sQuery(id+"F0.wireOp",EDGE,"E83.2.0.0")}),-1.0]])]});
            var Q11;
            Q11=makeQuery(id+"F0.imprint","IMPRINT",FACE,{"disambiguationData":[TD([[makeQuery(id+"F0.imprint","IMPRINT",EDGE,{"derivedFrom":sQuery(id+"F0.wireOp",EDGE,"E83.3.0.0")}),-1.0]])]});
            var Q12;
            Q12=makeQuery(id+"F0.imprint","IMPRINT",FACE,{"disambiguationData":[TD([[makeQuery(id+"F0.imprint","IMPRINT",EDGE,{"derivedFrom":sQuery(id+"F0.wireOp",EDGE,"E25.MirrorCS")}),1.0]])]});
            var Q13;
            Q13=makeQuery(id+"F0.imprint","IMPRINT",FACE,{"disambiguationData":[TD([[makeQuery(id+"F0.imprint","IMPRINT",EDGE,{"derivedFrom":sQuery(id+"F0.wireOp",EDGE,"E5.MirrorCS")}),1.0]])]});
            var Q14;
            Q14=makeQuery(id+"F0.imprint","IMPRINT",FACE,{"disambiguationData":[TD([[makeQuery(id+"F0.imprint","IMPRINT",EDGE,{"derivedFrom":sQuery(id+"F0.wireOp",EDGE,"E6.MirrorCS")}),-1.0]])]});
            var Q15;
            Q15=makeQuery(id+"F0.imprint","IMPRINT",FACE,{"disambiguationData":[TD([[makeQuery(id+"F0.imprint","IMPRINT",EDGE,{"derivedFrom":sQuery(id+"F0.wireOp",EDGE,"E8.MirrorCS")}),-1.0]])]});
            var Q16;
            Q16=makeQuery(id+"F0.imprint","IMPRINT",FACE,{"disambiguationData":[TD([[makeQuery(id+"F0.imprint","IMPRINT",EDGE,{"derivedFrom":sQuery(id+"F0.wireOp",EDGE,"E4.MirrorCS")}),-1.0]])]});
            var Q17;
            Q17=makeQuery(id+"F0.imprint","IMPRINT",FACE,{"disambiguationData":[TD([[makeQuery(id+"F0.imprint","IMPRINT",EDGE,{"derivedFrom":sQuery(id+"F0.wireOp",EDGE,"E12.MirrorCS")}),1.0]])]});
            var Q18;
            Q18=makeQuery(id+"F0.imprint","IMPRINT",FACE,{"disambiguationData":[TD([[makeQuery(id+"F0.imprint","IMPRINT",EDGE,{"derivedFrom":sQuery(id+"F0.wireOp",EDGE,"E83.3.1.0")}),-1.0]])]});
            var Q19;
            Q19=makeQuery(id+"F0.imprint","IMPRINT",FACE,{"disambiguationData":[TD([[makeQuery(id+"F0.imprint","IMPRINT",EDGE,{"derivedFrom":sQuery(id+"F0.wireOp",EDGE,"E83.2.1.0")}),-1.0]])]});
            var Q20;
            Q20=makeQuery(id+"F0.imprint","IMPRINT",FACE,{"disambiguationData":[TD([[makeQuery(id+"F0.imprint","IMPRINT",EDGE,{"derivedFrom":sQuery(id+"F0.wireOp",EDGE,"E83.1.1.0")}),-1.0]])]});
            var Q21;
            Q21=makeQuery(id+"F0.imprint","IMPRINT",FACE,{"disambiguationData":[TD([[makeQuery(id+"F0.imprint","IMPRINT",EDGE,{"derivedFrom":sQuery(id+"F0.wireOp",EDGE,"E83.0.1.0")}),-1.0]])]});
            var Q22;
            Q22=makeQuery(id+"F0.imprint","IMPRINT",FACE,{"disambiguationData":[TD([[makeQuery(id+"F0.imprint","IMPRINT",EDGE,{"derivedFrom":sQuery(id+"F0.wireOp",EDGE,"E3.2.1.0")}),-1.0]])]});
            var Q23;
            Q23=makeQuery(id+"F0.imprint","IMPRINT",FACE,{"disambiguationData":[TD([[makeQuery(id+"F0.imprint","IMPRINT",EDGE,{"derivedFrom":sQuery(id+"F0.wireOp",EDGE,"E3.1.1.0")}),-1.0]])]});
            var Q24;
            Q24=makeQuery(id+"F0.imprint","IMPRINT",FACE,{"disambiguationData":[TD([[makeQuery(id+"F0.imprint","IMPRINT",EDGE,{"derivedFrom":sQuery(id+"F0.wireOp",EDGE,"E3.0.1.0")}),-1.0]])]});
            var Q25;
            Q25=makeQuery(id+"F0.imprint","IMPRINT",FACE,{"disambiguationData":[TD([[makeQuery(id+"F0.imprint","IMPRINT",EDGE,{"derivedFrom":sQuery(id+"F0.wireOp",EDGE,"E3.0.2.0")}),-1.0]])]});
            var Q26;
            Q26=makeQuery(id+"F0.imprint","IMPRINT",FACE,{"disambiguationData":[TD([[makeQuery(id+"F0.imprint","IMPRINT",EDGE,{"derivedFrom":sQuery(id+"F0.wireOp",EDGE,"E3.1.2.0")}),-1.0]])]});
            var Q27;
            Q27=makeQuery(id+"F0.imprint","IMPRINT",FACE,{"disambiguationData":[TD([[makeQuery(id+"F0.imprint","IMPRINT",EDGE,{"derivedFrom":sQuery(id+"F0.wireOp",EDGE,"E3.2.2.0")}),-1.0]])]});
            var Q28;
            Q28=makeQuery(id+"F0.imprint","IMPRINT",FACE,{"disambiguationData":[TD([[makeQuery(id+"F0.imprint","IMPRINT",EDGE,{"derivedFrom":sQuery(id+"F0.wireOp",EDGE,"E83.0.2.0")}),-1.0]])]});
            var Q29;
            Q29=makeQuery(id+"F0.imprint","IMPRINT",FACE,{"disambiguationData":[TD([[makeQuery(id+"F0.imprint","IMPRINT",EDGE,{"derivedFrom":sQuery(id+"F0.wireOp",EDGE,"E83.1.2.0")}),-1.0]])]});
            var Q30;
            Q30=makeQuery(id+"F0.imprint","IMPRINT",FACE,{"disambiguationData":[TD([[makeQuery(id+"F0.imprint","IMPRINT",EDGE,{"derivedFrom":sQuery(id+"F0.wireOp",EDGE,"E83.2.2.0")}),-1.0]])]});
            var Q31;
            Q31=makeQuery(id+"F0.imprint","IMPRINT",FACE,{"disambiguationData":[TD([[makeQuery(id+"F0.imprint","IMPRINT",EDGE,{"derivedFrom":sQuery(id+"F0.wireOp",EDGE,"E83.3.2.0")}),-1.0]])]});
            var Q32;
            Q32=makeQuery(id+"F0.imprint","IMPRINT",FACE,{"disambiguationData":[TD([[makeQuery(id+"F0.imprint","IMPRINT",EDGE,{"derivedFrom":sQuery(id+"F0.wireOp",EDGE,"E22.MirrorCS")}),1.0]])]});
            var Q33;
            Q33=makeQuery(id+"F0.imprint","IMPRINT",FACE,{"disambiguationData":[TD([[makeQuery(id+"F0.imprint","IMPRINT",EDGE,{"derivedFrom":sQuery(id+"F0.wireOp",EDGE,"E26.MirrorCS")}),1.0]])]});
            var Q34;
            Q34=makeQuery(id+"F0.imprint","IMPRINT",FACE,{"disambiguationData":[TD([[makeQuery(id+"F0.imprint","IMPRINT",EDGE,{"derivedFrom":sQuery(id+"F0.wireOp",EDGE,"E24.MirrorCS")}),1.0]])]});
            var Q35;
            Q35=makeQuery(id+"F0.imprint","IMPRINT",FACE,{"disambiguationData":[TD([[makeQuery(id+"F0.imprint","IMPRINT",EDGE,{"derivedFrom":sQuery(id+"F0.wireOp",EDGE,"E3.0.3.0")}),-1.0]])]});
            var Q36;
            Q36=makeQuery(id+"F0.imprint","IMPRINT",FACE,{"disambiguationData":[TD([[makeQuery(id+"F0.imprint","IMPRINT",EDGE,{"derivedFrom":sQuery(id+"F0.wireOp",EDGE,"E3.1.3.0")}),-1.0]])]});
            var Q37;
            Q37=makeQuery(id+"F0.imprint","IMPRINT",FACE,{"disambiguationData":[TD([[makeQuery(id+"F0.imprint","IMPRINT",EDGE,{"derivedFrom":sQuery(id+"F0.wireOp",EDGE,"E3.2.3.0")}),-1.0]])]});
            var Q38;
            Q38=makeQuery(id+"F0.imprint","IMPRINT",FACE,{"disambiguationData":[TD([[makeQuery(id+"F0.imprint","IMPRINT",EDGE,{"derivedFrom":sQuery(id+"F0.wireOp",EDGE,"E83.0.3.0")}),-1.0]])]});
            var Q39;
            Q39=makeQuery(id+"F0.imprint","IMPRINT",FACE,{"disambiguationData":[TD([[makeQuery(id+"F0.imprint","IMPRINT",EDGE,{"derivedFrom":sQuery(id+"F0.wireOp",EDGE,"E83.1.3.0")}),-1.0]])]});
            var Q40;
            Q40=makeQuery(id+"F0.imprint","IMPRINT",FACE,{"disambiguationData":[TD([[makeQuery(id+"F0.imprint","IMPRINT",EDGE,{"derivedFrom":sQuery(id+"F0.wireOp",EDGE,"E83.2.3.0")}),-1.0]])]});
            var Q41;
            Q41=makeQuery(id+"F0.imprint","IMPRINT",FACE,{"disambiguationData":[TD([[makeQuery(id+"F0.imprint","IMPRINT",EDGE,{"derivedFrom":sQuery(id+"F0.wireOp",EDGE,"E83.3.3.0")}),-1.0]])]});
            var Q42;
            Q42=makeQuery(id+"F0.imprint","IMPRINT",FACE,{"disambiguationData":[TD([[makeQuery(id+"F0.imprint","IMPRINT",EDGE,{"derivedFrom":sQuery(id+"F0.wireOp",EDGE,"E9.MirrorCS")}),1.0]])]});
            var Q43;
            Q43=makeQuery(id+"F0.imprint","IMPRINT",FACE,{"disambiguationData":[TD([[makeQuery(id+"F0.imprint","IMPRINT",EDGE,{"derivedFrom":sQuery(id+"F0.wireOp",EDGE,"E13.MirrorCS")}),1.0]])]});
            var Q44;
            Q44=makeQuery(id+"F0.imprint","IMPRINT",FACE,{"disambiguationData":[TD([[makeQuery(id+"F0.imprint","IMPRINT",EDGE,{"derivedFrom":sQuery(id+"F0.wireOp",EDGE,"E15.MirrorCS")}),-1.0]])]});
            var Q45;
            Q45=makeQuery(id+"F0.imprint","IMPRINT",FACE,{"disambiguationData":[TD([[makeQuery(id+"F0.imprint","IMPRINT",EDGE,{"derivedFrom":sQuery(id+"F0.wireOp",EDGE,"E27.MirrorCS")}),1.0]])]});
            var Q46;
            Q46=makeQuery(id+"F0.imprint","IMPRINT",FACE,{"disambiguationData":[TD([[makeQuery(id+"F0.imprint","IMPRINT",EDGE,{"derivedFrom":sQuery(id+"F0.wireOp",EDGE,"E23.MirrorCS")}),1.0]])]});
            var Q47;
            Q47=makeQuery(id+"F0.imprint","IMPRINT",FACE,{"disambiguationData":[TD([[makeQuery(id+"F0.imprint","IMPRINT",EDGE,{"derivedFrom":sQuery(id+"F0.wireOp",EDGE,"E28.MirrorCS")}),1.0]])]});
            var Q48;
            Q48=makeQuery(id+"F0.imprint","IMPRINT",FACE,{"disambiguationData":[TD([[makeQuery(id+"F0.imprint","IMPRINT",EDGE,{"derivedFrom":sQuery(id+"F0.wireOp",EDGE,"E83.3.4.0")}),-1.0]])]});
            var Q49;
            Q49=makeQuery(id+"F0.imprint","IMPRINT",FACE,{"disambiguationData":[TD([[makeQuery(id+"F0.imprint","IMPRINT",EDGE,{"derivedFrom":sQuery(id+"F0.wireOp",EDGE,"E83.2.4.0")}),-1.0]])]});
            var Q50;
            Q50=makeQuery(id+"F0.imprint","IMPRINT",FACE,{"disambiguationData":[TD([[makeQuery(id+"F0.imprint","IMPRINT",EDGE,{"derivedFrom":sQuery(id+"F0.wireOp",EDGE,"E83.1.4.0")}),-1.0]])]});
            var Q51;
            Q51=makeQuery(id+"F0.imprint","IMPRINT",FACE,{"disambiguationData":[TD([[makeQuery(id+"F0.imprint","IMPRINT",EDGE,{"derivedFrom":sQuery(id+"F0.wireOp",EDGE,"E83.0.4.0")}),-1.0]])]});
            var Q52;
            Q52=makeQuery(id+"F0.imprint","IMPRINT",FACE,{"disambiguationData":[TD([[makeQuery(id+"F0.imprint","IMPRINT",EDGE,{"derivedFrom":sQuery(id+"F0.wireOp",EDGE,"E3.2.4.0")}),-1.0]])]});
            var Q53;
            Q53=makeQuery(id+"F0.imprint","IMPRINT",FACE,{"disambiguationData":[TD([[makeQuery(id+"F0.imprint","IMPRINT",EDGE,{"derivedFrom":sQuery(id+"F0.wireOp",EDGE,"E3.1.4.0")}),-1.0]])]});
            var Q54;
            Q54=makeQuery(id+"F0.imprint","IMPRINT",FACE,{"disambiguationData":[TD([[makeQuery(id+"F0.imprint","IMPRINT",EDGE,{"derivedFrom":sQuery(id+"F0.wireOp",EDGE,"E3.0.4.0")}),-1.0]])]});
            var Q55;
            Q55=makeQuery(id+"F0.imprint","IMPRINT",FACE,{"disambiguationData":[TD([[makeQuery(id+"F0.imprint","IMPRINT",EDGE,{"derivedFrom":sQuery(id+"F0.wireOp",EDGE,"E3.0.5.0")}),-1.0]])]});
            var Q56;
            Q56=makeQuery(id+"F0.imprint","IMPRINT",FACE,{"disambiguationData":[TD([[makeQuery(id+"F0.imprint","IMPRINT",EDGE,{"derivedFrom":sQuery(id+"F0.wireOp",EDGE,"E3.1.5.0")}),-1.0]])]});
            var Q57;
            Q57=makeQuery(id+"F0.imprint","IMPRINT",FACE,{"disambiguationData":[TD([[makeQuery(id+"F0.imprint","IMPRINT",EDGE,{"derivedFrom":sQuery(id+"F0.wireOp",EDGE,"E3.2.5.0")}),-1.0]])]});
            var Q58;
            Q58=makeQuery(id+"F0.imprint","IMPRINT",FACE,{"disambiguationData":[TD([[makeQuery(id+"F0.imprint","IMPRINT",EDGE,{"derivedFrom":sQuery(id+"F0.wireOp",EDGE,"E83.0.5.0")}),-1.0]])]});
            var Q59;
            Q59=makeQuery(id+"F0.imprint","IMPRINT",FACE,{"disambiguationData":[TD([[makeQuery(id+"F0.imprint","IMPRINT",EDGE,{"derivedFrom":sQuery(id+"F0.wireOp",EDGE,"E83.1.5.0")}),-1.0]])]});
            var Q60;
            Q60=makeQuery(id+"F0.imprint","IMPRINT",FACE,{"disambiguationData":[TD([[makeQuery(id+"F0.imprint","IMPRINT",EDGE,{"derivedFrom":sQuery(id+"F0.wireOp",EDGE,"E83.2.5.0")}),-1.0]])]});
            var Q61;
            Q61=makeQuery(id+"F0.imprint","IMPRINT",FACE,{"disambiguationData":[TD([[makeQuery(id+"F0.imprint","IMPRINT",EDGE,{"derivedFrom":sQuery(id+"F0.wireOp",EDGE,"E83.3.5.0")}),-1.0]])]});
            var Q62;
            Q62=makeQuery(id+"F0.imprint","IMPRINT",FACE,{"disambiguationData":[TD([[makeQuery(id+"F0.imprint","IMPRINT",EDGE,{"derivedFrom":sQuery(id+"F0.wireOp",EDGE,"E14.MirrorCS")}),1.0]])]});
            var Q63;
            Q63=makeQuery(id+"F0.imprint","IMPRINT",FACE,{"disambiguationData":[TD([[makeQuery(id+"F0.imprint","IMPRINT",EDGE,{"derivedFrom":sQuery(id+"F0.wireOp",EDGE,"E10.MirrorCS")}),1.0]])]});
            var Q64;
            Q64=makeQuery(id+"F0.imprint","IMPRINT",FACE,{"disambiguationData":[TD([[makeQuery(id+"F0.imprint","IMPRINT",EDGE,{"derivedFrom":sQuery(id+"F0.wireOp",EDGE,"E20.MirrorCS")}),-1.0]])]});
            var Q65;
            Q65=makeQuery(id+"F0.imprint","IMPRINT",FACE,{"disambiguationData":[TD([[makeQuery(id+"F0.imprint","IMPRINT",EDGE,{"derivedFrom":sQuery(id+"F0.wireOp",EDGE,"E79.bottom")}),1.0]])]});
            var Q66;
            Q66=makeQuery(id+"F0.imprint","IMPRINT",FACE,{"disambiguationData":[TD([[makeQuery(id+"F0.imprint","IMPRINT",EDGE,{"derivedFrom":sQuery(id+"F0.wireOp",EDGE,"E80.bottom")}),1.0]])]});
            var Q67;
            Q67=makeQuery(id+"F0.imprint","IMPRINT",FACE,{"disambiguationData":[TD([[makeQuery(id+"F0.imprint","IMPRINT",EDGE,{"derivedFrom":sQuery(id+"F0.wireOp",EDGE,"E81.bottom")}),1.0]])]});
            var Q68;
            Q68=makeQuery(id+"F0.imprint","IMPRINT",FACE,{"disambiguationData":[TD([[makeQuery(id+"F0.imprint","IMPRINT",EDGE,{"derivedFrom":sQuery(id+"F0.wireOp",EDGE,"E84.bottom")}),1.0]])]});
            var Q69;
            Q69=makeQuery(id+"F0.imprint","IMPRINT",FACE,{"disambiguationData":[TD([[makeQuery(id+"F0.imprint","IMPRINT",EDGE,{"derivedFrom":sQuery(id+"F0.wireOp",EDGE,"E85.bottom")}),1.0]])]});
            var Q70;
            Q70=makeQuery(id+"F0.imprint","IMPRINT",FACE,{"disambiguationData":[TD([[makeQuery(id+"F0.imprint","IMPRINT",EDGE,{"derivedFrom":sQuery(id+"F0.wireOp",EDGE,"E86.bottom")}),1.0]])]});
            var Q71;
            Q71=makeQuery(id+"F0.imprint","IMPRINT",FACE,{"disambiguationData":[TD([[makeQuery(id+"F0.imprint","IMPRINT",EDGE,{"derivedFrom":sQuery(id+"F0.wireOp",EDGE,"E87.bottom")}),1.0]])]});
            var Q72;
            Q72=makeQuery(id+"F0.imprint","IMPRINT",FACE,{"disambiguationData":[TD([[makeQuery(id+"F0.imprint","IMPRINT",EDGE,{"derivedFrom":sQuery(id+"F0.wireOp",EDGE,"E78.bottom")}),-1.0]])]});
            var Q73;
            Q73=makeQuery(id+"F0.imprint","IMPRINT",FACE,{"disambiguationData":[TD([[makeQuery(id+"F0.imprint","IMPRINT",EDGE,{"derivedFrom":sQuery(id+"F0.wireOp",EDGE,"E77.bottom")}),-1.0]])]});
            var Q74;
            Q74=makeQuery(id+"F0.imprint","IMPRINT",FACE,{"disambiguationData":[TD([[makeQuery(id+"F0.imprint","IMPRINT",EDGE,{"derivedFrom":sQuery(id+"F0.wireOp",EDGE,"E76.bottom")}),-1.0]])]});
            extrude(context, id + "F5", {"entities" : qUnion([Q0, Q1, Q2, Q3, Q4, Q5, Q6, Q7, Q8, Q9, Q10, Q11, Q12, Q13, Q14, Q15, Q16, Q17, Q18, Q19, Q20, Q21, Q22, Q23, Q24, Q25, Q26, Q27, Q28, Q29, Q30, Q31, Q32, Q33, Q34, Q35, Q36, Q37, Q38, Q39, Q40, Q41, Q42, Q43, Q44, Q45, Q46, Q47, Q48, Q49, Q50, Q51, Q52, Q53, Q54, Q55, Q56, Q57, Q58, Q59, Q60, Q61, Q62, Q63, Q64, Q65, Q66, Q67, Q68, Q69, Q70, Q71, Q72, Q73, Q74]), "depth" : 152.4 * mm});
        }
        {
            var Q0;
            Q0=qCreatedBy(makeId("Front.planeOp"),FACE);
            var sketch = newSketch(context, id + "F6", { "sketchPlane" : qUnion([Q0])});
            skLineSegment(sketch, "E97", {"start": v(-14993.77, 810.64) * mm, "end": v(-10091.57, 810.64) * mm});
            skLineSegment(sketch, "E98", {"start": v(-10091.57, 810.64) * mm, "end": v(-10091.57, 1262.75) * mm});
            skLineSegment(sketch, "E99", {"start": v(-10091.57, 1262.75) * mm, "end": v(-11201.14, 1420.24) * mm});
            skLineSegment(sketch, "E100", {"start": v(-11201.14, 1420.24) * mm, "end": v(-11874.03, 1953.64) * mm});
            skLineSegment(sketch, "E101", {"start": v(-11874.03, 1953.64) * mm, "end": v(-14027.8, 1953.64) * mm});
            skLineSegment(sketch, "E102", {"start": v(-14027.8, 1953.64) * mm, "end": v(-14664.22, 1420.24) * mm});
            skLineSegment(sketch, "E103", {"start": v(-14664.22, 1420.24) * mm, "end": v(-14993.77, 1420.24) * mm});
            skLineSegment(sketch, "E104", {"start": v(-14993.77, 1420.24) * mm, "end": v(-14993.77, 810.64) * mm});
            skCircle(sketch, "E105", {"center": v(-14136.12, 810.64) * mm, "radius": 330.2 * mm});
            skCircle(sketch, "E106", {"center": v(-10929.11, 810.64) * mm, "radius": 330.2 * mm});
            skSolve(sketch);
        }
        {
            var Q0;
            {var subQ8=sQuery(id+"F6.wireOp",EDGE,"E98");Q0=makeQuery(id+"F6.imprint","IMPRINT",FACE,{"disambiguationData":[TD([[makeQuery(id+"F6.imprint","IMPRINT",EDGE,{"derivedFrom":subQ8}),1.0]])]});}
            var Q1;
            {var subQ0=sQuery(id+"F6.wireOp",EDGE,"E105");var subQ1=sQuery(id+"F6.wireOp",EDGE,"E97");var subQ3=makeQuery(id+"F6.imprint","INTERSECT",VERTEX,{"disambiguationData":[OD(0.0)],"derivedFrom":[subQ1,subQ0]});Q1=makeQuery(id+"F6.imprint","IMPRINT",FACE,{"disambiguationData":[TD([[makeQuery(id+"F6.imprint","IMPRINT",EDGE,{"disambiguationData":[TD([[subQ3,-1.0]])],"derivedFrom":subQ1}),1.0]])]});}
            var Q2;
            {var subQ0=sQuery(id+"F6.wireOp",EDGE,"E106");var subQ1=sQuery(id+"F6.wireOp",EDGE,"E97");var subQ3=makeQuery(id+"F6.imprint","INTERSECT",VERTEX,{"disambiguationData":[OD(0.0)],"derivedFrom":[subQ1,subQ0]});Q2=makeQuery(id+"F6.imprint","IMPRINT",FACE,{"disambiguationData":[TD([[makeQuery(id+"F6.imprint","IMPRINT",EDGE,{"disambiguationData":[TD([[subQ3,-1.0]])],"derivedFrom":subQ1}),1.0]])]});}
            var Q3;
            {var subQ0=sQuery(id+"F6.wireOp",EDGE,"E105");var subQ1=sQuery(id+"F6.wireOp",EDGE,"E97");var subQ3=makeQuery(id+"F6.imprint","INTERSECT",VERTEX,{"disambiguationData":[OD(0.0)],"derivedFrom":[subQ1,subQ0]});Q3=makeQuery(id+"F6.imprint","IMPRINT",FACE,{"disambiguationData":[TD([[makeQuery(id+"F6.imprint","IMPRINT",EDGE,{"disambiguationData":[TD([[subQ3,-1.0]])],"derivedFrom":subQ1}),-1.0]])]});}
            var Q4;
            {var subQ0=sQuery(id+"F6.wireOp",EDGE,"E106");var subQ1=sQuery(id+"F6.wireOp",EDGE,"E97");var subQ3=makeQuery(id+"F6.imprint","INTERSECT",VERTEX,{"disambiguationData":[OD(0.0)],"derivedFrom":[subQ1,subQ0]});Q4=makeQuery(id+"F6.imprint","IMPRINT",FACE,{"disambiguationData":[TD([[makeQuery(id+"F6.imprint","IMPRINT",EDGE,{"disambiguationData":[TD([[subQ3,-1.0]])],"derivedFrom":subQ1}),-1.0]])]});}
            extrude(context, id + "F7", {"entities" : qUnion([Q0, Q1, Q2, Q3, Q4]), "depth" : 30.48 * mm});
        }
        {
            var Q0;
            Q0=makeQuery(id+"F2.opExtrude","SWEPT_BODY",BODY,{"disambiguationData":[OSD([sQuery(id+"F0.wireOp",EDGE,"E1.bottom"),sQuery(id+"F0.wireOp",EDGE,"E1.top"),sQuery(id+"F0.wireOp",EDGE,"E1.left"),sQuery(id+"F0.wireOp",EDGE,"E1.right"),sQuery(id+"F0.wireOp",EDGE,"E2.bottom"),sQuery(id+"F0.wireOp",EDGE,"E2.top"),sQuery(id+"F0.wireOp",EDGE,"E2.left"),sQuery(id+"F0.wireOp",EDGE,"E2.right"),sQuery(id+"F0.wireOp",EDGE,"E3.0.1.0"),sQuery(id+"F0.wireOp",EDGE,"E3.0.1.1"),sQuery(id+"F0.wireOp",EDGE,"E3.0.1.2"),sQuery(id+"F0.wireOp",EDGE,"E3.0.1.3"),sQuery(id+"F0.wireOp",EDGE,"E3.0.2.0"),sQuery(id+"F0.wireOp",EDGE,"E3.0.2.1"),sQuery(id+"F0.wireOp",EDGE,"E3.0.2.2"),sQuery(id+"F0.wireOp",EDGE,"E3.0.2.3"),sQuery(id+"F0.wireOp",EDGE,"E3.0.3.0"),sQuery(id+"F0.wireOp",EDGE,"E3.0.3.1"),sQuery(id+"F0.wireOp",EDGE,"E3.0.3.2"),sQuery(id+"F0.wireOp",EDGE,"E3.0.3.3"),sQuery(id+"F0.wireOp",EDGE,"E3.0.4.0"),sQuery(id+"F0.wireOp",EDGE,"E3.0.4.1"),sQuery(id+"F0.wireOp",EDGE,"E3.0.4.2"),sQuery(id+"F0.wireOp",EDGE,"E3.0.4.3"),sQuery(id+"F0.wireOp",EDGE,"E3.0.5.0"),sQuery(id+"F0.wireOp",EDGE,"E3.0.5.1"),sQuery(id+"F0.wireOp",EDGE,"E3.0.5.2"),sQuery(id+"F0.wireOp",EDGE,"E3.0.5.3"),sQuery(id+"F0.wireOp",EDGE,"E3.1.0.0"),sQuery(id+"F0.wireOp",EDGE,"E3.1.0.1"),sQuery(id+"F0.wireOp",EDGE,"E3.1.0.2"),sQuery(id+"F0.wireOp",EDGE,"E3.1.0.3"),sQuery(id+"F0.wireOp",EDGE,"E3.1.1.0"),sQuery(id+"F0.wireOp",EDGE,"E3.1.1.1"),sQuery(id+"F0.wireOp",EDGE,"E3.1.1.2"),sQuery(id+"F0.wireOp",EDGE,"E3.1.1.3"),sQuery(id+"F0.wireOp",EDGE,"E3.1.2.0"),sQuery(id+"F0.wireOp",EDGE,"E3.1.2.1"),sQuery(id+"F0.wireOp",EDGE,"E3.1.2.2"),sQuery(id+"F0.wireOp",EDGE,"E3.1.2.3"),sQuery(id+"F0.wireOp",EDGE,"E3.1.3.0"),sQuery(id+"F0.wireOp",EDGE,"E3.1.3.1"),sQuery(id+"F0.wireOp",EDGE,"E3.1.3.2"),sQuery(id+"F0.wireOp",EDGE,"E3.1.3.3"),sQuery(id+"F0.wireOp",EDGE,"E3.1.4.0"),sQuery(id+"F0.wireOp",EDGE,"E3.1.4.1"),sQuery(id+"F0.wireOp",EDGE,"E3.1.4.2"),sQuery(id+"F0.wireOp",EDGE,"E3.1.4.3"),sQuery(id+"F0.wireOp",EDGE,"E3.1.5.0"),sQuery(id+"F0.wireOp",EDGE,"E3.1.5.1"),sQuery(id+"F0.wireOp",EDGE,"E3.1.5.2"),sQuery(id+"F0.wireOp",EDGE,"E3.1.5.3"),sQuery(id+"F0.wireOp",EDGE,"E3.2.0.0"),sQuery(id+"F0.wireOp",EDGE,"E3.2.0.1"),sQuery(id+"F0.wireOp",EDGE,"E3.2.0.2"),sQuery(id+"F0.wireOp",EDGE,"E3.2.0.3"),sQuery(id+"F0.wireOp",EDGE,"E3.2.1.0"),sQuery(id+"F0.wireOp",EDGE,"E3.2.1.1"),sQuery(id+"F0.wireOp",EDGE,"E3.2.1.2"),sQuery(id+"F0.wireOp",EDGE,"E3.2.1.3"),sQuery(id+"F0.wireOp",EDGE,"E3.2.2.0"),sQuery(id+"F0.wireOp",EDGE,"E3.2.2.1"),sQuery(id+"F0.wireOp",EDGE,"E3.2.2.2"),sQuery(id+"F0.wireOp",EDGE,"E3.2.2.3"),sQuery(id+"F0.wireOp",EDGE,"E3.2.3.0"),sQuery(id+"F0.wireOp",EDGE,"E3.2.3.1"),sQuery(id+"F0.wireOp",EDGE,"E3.2.3.2"),sQuery(id+"F0.wireOp",EDGE,"E3.2.3.3"),sQuery(id+"F0.wireOp",EDGE,"E3.2.4.0"),sQuery(id+"F0.wireOp",EDGE,"E3.2.4.1"),sQuery(id+"F0.wireOp",EDGE,"E3.2.4.2"),sQuery(id+"F0.wireOp",EDGE,"E3.2.4.3"),sQuery(id+"F0.wireOp",EDGE,"E3.2.5.0"),sQuery(id+"F0.wireOp",EDGE,"E3.2.5.1"),sQuery(id+"F0.wireOp",EDGE,"E3.2.5.2"),sQuery(id+"F0.wireOp",EDGE,"E3.2.5.3"),sQuery(id+"F0.wireOp",EDGE,"E4.MirrorCS"),sQuery(id+"F0.wireOp",EDGE,"E5.MirrorCS"),sQuery(id+"F0.wireOp",EDGE,"E6.MirrorCS"),sQuery(id+"F0.wireOp",EDGE,"E7.MirrorCS"),sQuery(id+"F0.wireOp",EDGE,"E8.MirrorCS"),sQuery(id+"F0.wireOp",EDGE,"E9.MirrorCS"),sQuery(id+"F0.wireOp",EDGE,"E10.MirrorCS"),sQuery(id+"F0.wireOp",EDGE,"E11.MirrorCS"),sQuery(id+"F0.wireOp",EDGE,"E12.MirrorCS"),sQuery(id+"F0.wireOp",EDGE,"E13.MirrorCS"),sQuery(id+"F0.wireOp",EDGE,"E14.MirrorCS"),sQuery(id+"F0.wireOp",EDGE,"E15.MirrorCS"),sQuery(id+"F0.wireOp",EDGE,"E16.MirrorCS"),sQuery(id+"F0.wireOp",EDGE,"E17.MirrorCS"),sQuery(id+"F0.wireOp",EDGE,"E18.MirrorCS"),sQuery(id+"F0.wireOp",EDGE,"E19.MirrorCS"),sQuery(id+"F0.wireOp",EDGE,"E20.MirrorCS"),sQuery(id+"F0.wireOp",EDGE,"E21.MirrorCS"),sQuery(id+"F0.wireOp",EDGE,"E22.MirrorCS"),sQuery(id+"F0.wireOp",EDGE,"E23.MirrorCS"),sQuery(id+"F0.wireOp",EDGE,"E24.MirrorCS"),sQuery(id+"F0.wireOp",EDGE,"E25.MirrorCS"),sQuery(id+"F0.wireOp",EDGE,"E26.MirrorCS"),sQuery(id+"F0.wireOp",EDGE,"E27.MirrorCS"),sQuery(id+"F0.wireOp",EDGE,"E28.MirrorCS"),sQuery(id+"F0.wireOp",EDGE,"E29.MirrorCS"),sQuery(id+"F0.wireOp",EDGE,"E30.MirrorCS"),sQuery(id+"F0.wireOp",EDGE,"E31.MirrorCS"),sQuery(id+"F0.wireOp",EDGE,"E32.MirrorCS"),sQuery(id+"F0.wireOp",EDGE,"E33.MirrorCS"),sQuery(id+"F0.wireOp",EDGE,"E34.MirrorCS"),sQuery(id+"F0.wireOp",EDGE,"E35.MirrorCS"),sQuery(id+"F0.wireOp",EDGE,"E36.MirrorCS"),sQuery(id+"F0.wireOp",EDGE,"E37.MirrorCS"),sQuery(id+"F0.wireOp",EDGE,"E38.MirrorCS"),sQuery(id+"F0.wireOp",EDGE,"E39.MirrorCS"),sQuery(id+"F0.wireOp",EDGE,"E40.MirrorCS"),sQuery(id+"F0.wireOp",EDGE,"E41.MirrorCS"),sQuery(id+"F0.wireOp",EDGE,"E42.MirrorCS"),sQuery(id+"F0.wireOp",EDGE,"E43.MirrorCS"),sQuery(id+"F0.wireOp",EDGE,"E44.MirrorCS"),sQuery(id+"F0.wireOp",EDGE,"E45.MirrorCS"),sQuery(id+"F0.wireOp",EDGE,"E46.MirrorCS"),sQuery(id+"F0.wireOp",EDGE,"E47.MirrorCS"),sQuery(id+"F0.wireOp",EDGE,"E48.MirrorCS"),sQuery(id+"F0.wireOp",EDGE,"E49.MirrorCS"),sQuery(id+"F0.wireOp",EDGE,"E50.MirrorCS"),sQuery(id+"F0.wireOp",EDGE,"E51.MirrorCS"),sQuery(id+"F0.wireOp",EDGE,"E52.MirrorCS"),sQuery(id+"F0.wireOp",EDGE,"E53.MirrorCS"),sQuery(id+"F0.wireOp",EDGE,"E54.MirrorCS"),sQuery(id+"F0.wireOp",EDGE,"E55.MirrorCS"),sQuery(id+"F0.wireOp",EDGE,"E56.MirrorCS"),sQuery(id+"F0.wireOp",EDGE,"E57.MirrorCS"),sQuery(id+"F0.wireOp",EDGE,"E58.MirrorCS"),sQuery(id+"F0.wireOp",EDGE,"E59.MirrorCS"),sQuery(id+"F0.wireOp",EDGE,"E60.MirrorCS"),sQuery(id+"F0.wireOp",EDGE,"E61.MirrorCS"),sQuery(id+"F0.wireOp",EDGE,"E62.MirrorCS"),sQuery(id+"F0.wireOp",EDGE,"E63.MirrorCS"),sQuery(id+"F0.wireOp",EDGE,"E64.MirrorCS"),sQuery(id+"F0.wireOp",EDGE,"E65.MirrorCS"),sQuery(id+"F0.wireOp",EDGE,"E66.MirrorCS"),sQuery(id+"F0.wireOp",EDGE,"E67.MirrorCS"),sQuery(id+"F0.wireOp",EDGE,"E68.MirrorCS"),sQuery(id+"F0.wireOp",EDGE,"E69.MirrorCS"),sQuery(id+"F0.wireOp",EDGE,"E70.MirrorCS"),sQuery(id+"F0.wireOp",EDGE,"E71.MirrorCS"),sQuery(id+"F0.wireOp",EDGE,"E72.MirrorCS"),sQuery(id+"F0.wireOp",EDGE,"E73.MirrorCS"),sQuery(id+"F0.wireOp",EDGE,"E74.MirrorCS"),sQuery(id+"F0.wireOp",EDGE,"E75.MirrorCS"),sQuery(id+"F0.wireOp",EDGE,"E76.bottom"),sQuery(id+"F0.wireOp",EDGE,"E76.top"),sQuery(id+"F0.wireOp",EDGE,"E76.left"),sQuery(id+"F0.wireOp",EDGE,"E76.right"),sQuery(id+"F0.wireOp",EDGE,"E77.bottom"),sQuery(id+"F0.wireOp",EDGE,"E77.top"),sQuery(id+"F0.wireOp",EDGE,"E77.left"),sQuery(id+"F0.wireOp",EDGE,"E77.right"),sQuery(id+"F0.wireOp",EDGE,"E78.bottom"),sQuery(id+"F0.wireOp",EDGE,"E78.top"),sQuery(id+"F0.wireOp",EDGE,"E78.left"),sQuery(id+"F0.wireOp",EDGE,"E78.right"),sQuery(id+"F0.wireOp",EDGE,"E79.bottom"),sQuery(id+"F0.wireOp",EDGE,"E79.top"),sQuery(id+"F0.wireOp",EDGE,"E79.left"),sQuery(id+"F0.wireOp",EDGE,"E79.right"),sQuery(id+"F0.wireOp",EDGE,"E80.bottom"),sQuery(id+"F0.wireOp",EDGE,"E80.top"),sQuery(id+"F0.wireOp",EDGE,"E80.left"),sQuery(id+"F0.wireOp",EDGE,"E80.right"),sQuery(id+"F0.wireOp",EDGE,"E81.bottom"),sQuery(id+"F0.wireOp",EDGE,"E81.top"),sQuery(id+"F0.wireOp",EDGE,"E81.left"),sQuery(id+"F0.wireOp",EDGE,"E81.right"),sQuery(id+"F0.wireOp",EDGE,"E82.bottom"),sQuery(id+"F0.wireOp",EDGE,"E82.top"),sQuery(id+"F0.wireOp",EDGE,"E82.left"),sQuery(id+"F0.wireOp",EDGE,"E82.right"),sQuery(id+"F0.wireOp",EDGE,"E83.0.1.0"),sQuery(id+"F0.wireOp",EDGE,"E83.0.1.1"),sQuery(id+"F0.wireOp",EDGE,"E83.0.1.2"),sQuery(id+"F0.wireOp",EDGE,"E83.0.1.3"),sQuery(id+"F0.wireOp",EDGE,"E83.0.2.0"),sQuery(id+"F0.wireOp",EDGE,"E83.0.2.1"),sQuery(id+"F0.wireOp",EDGE,"E83.0.2.2"),sQuery(id+"F0.wireOp",EDGE,"E83.0.2.3"),sQuery(id+"F0.wireOp",EDGE,"E83.0.3.0"),sQuery(id+"F0.wireOp",EDGE,"E83.0.3.1"),sQuery(id+"F0.wireOp",EDGE,"E83.0.3.2"),sQuery(id+"F0.wireOp",EDGE,"E83.0.3.3"),sQuery(id+"F0.wireOp",EDGE,"E83.0.4.0"),sQuery(id+"F0.wireOp",EDGE,"E83.0.4.1"),sQuery(id+"F0.wireOp",EDGE,"E83.0.4.2"),sQuery(id+"F0.wireOp",EDGE,"E83.0.4.3"),sQuery(id+"F0.wireOp",EDGE,"E83.0.5.0"),sQuery(id+"F0.wireOp",EDGE,"E83.0.5.1"),sQuery(id+"F0.wireOp",EDGE,"E83.0.5.2"),sQuery(id+"F0.wireOp",EDGE,"E83.0.5.3"),sQuery(id+"F0.wireOp",EDGE,"E83.1.0.0"),sQuery(id+"F0.wireOp",EDGE,"E83.1.0.1"),sQuery(id+"F0.wireOp",EDGE,"E83.1.0.2"),sQuery(id+"F0.wireOp",EDGE,"E83.1.0.3"),sQuery(id+"F0.wireOp",EDGE,"E83.1.1.0"),sQuery(id+"F0.wireOp",EDGE,"E83.1.1.1"),sQuery(id+"F0.wireOp",EDGE,"E83.1.1.2"),sQuery(id+"F0.wireOp",EDGE,"E83.1.1.3"),sQuery(id+"F0.wireOp",EDGE,"E83.1.2.0"),sQuery(id+"F0.wireOp",EDGE,"E83.1.2.1"),sQuery(id+"F0.wireOp",EDGE,"E83.1.2.2"),sQuery(id+"F0.wireOp",EDGE,"E83.1.2.3"),sQuery(id+"F0.wireOp",EDGE,"E83.1.3.0"),sQuery(id+"F0.wireOp",EDGE,"E83.1.3.1"),sQuery(id+"F0.wireOp",EDGE,"E83.1.3.2"),sQuery(id+"F0.wireOp",EDGE,"E83.1.3.3"),sQuery(id+"F0.wireOp",EDGE,"E83.1.4.0"),sQuery(id+"F0.wireOp",EDGE,"E83.1.4.1"),sQuery(id+"F0.wireOp",EDGE,"E83.1.4.2"),sQuery(id+"F0.wireOp",EDGE,"E83.1.4.3"),sQuery(id+"F0.wireOp",EDGE,"E83.1.5.0"),sQuery(id+"F0.wireOp",EDGE,"E83.1.5.1"),sQuery(id+"F0.wireOp",EDGE,"E83.1.5.2"),sQuery(id+"F0.wireOp",EDGE,"E83.1.5.3"),sQuery(id+"F0.wireOp",EDGE,"E83.2.0.0"),sQuery(id+"F0.wireOp",EDGE,"E83.2.0.1"),sQuery(id+"F0.wireOp",EDGE,"E83.2.0.2"),sQuery(id+"F0.wireOp",EDGE,"E83.2.0.3"),sQuery(id+"F0.wireOp",EDGE,"E83.2.1.0"),sQuery(id+"F0.wireOp",EDGE,"E83.2.1.1"),sQuery(id+"F0.wireOp",EDGE,"E83.2.1.2"),sQuery(id+"F0.wireOp",EDGE,"E83.2.1.3"),sQuery(id+"F0.wireOp",EDGE,"E83.2.2.0"),sQuery(id+"F0.wireOp",EDGE,"E83.2.2.1"),sQuery(id+"F0.wireOp",EDGE,"E83.2.2.2"),sQuery(id+"F0.wireOp",EDGE,"E83.2.2.3"),sQuery(id+"F0.wireOp",EDGE,"E83.2.3.0"),sQuery(id+"F0.wireOp",EDGE,"E83.2.3.1"),sQuery(id+"F0.wireOp",EDGE,"E83.2.3.2"),sQuery(id+"F0.wireOp",EDGE,"E83.2.3.3"),sQuery(id+"F0.wireOp",EDGE,"E83.2.4.0"),sQuery(id+"F0.wireOp",EDGE,"E83.2.4.1"),sQuery(id+"F0.wireOp",EDGE,"E83.2.4.2"),sQuery(id+"F0.wireOp",EDGE,"E83.2.4.3"),sQuery(id+"F0.wireOp",EDGE,"E83.2.5.0"),sQuery(id+"F0.wireOp",EDGE,"E83.2.5.1"),sQuery(id+"F0.wireOp",EDGE,"E83.2.5.2"),sQuery(id+"F0.wireOp",EDGE,"E83.2.5.3"),sQuery(id+"F0.wireOp",EDGE,"E83.3.0.0"),sQuery(id+"F0.wireOp",EDGE,"E83.3.0.1"),sQuery(id+"F0.wireOp",EDGE,"E83.3.0.2"),sQuery(id+"F0.wireOp",EDGE,"E83.3.0.3"),sQuery(id+"F0.wireOp",EDGE,"E83.3.1.0"),sQuery(id+"F0.wireOp",EDGE,"E83.3.1.1"),sQuery(id+"F0.wireOp",EDGE,"E83.3.1.2"),sQuery(id+"F0.wireOp",EDGE,"E83.3.1.3"),sQuery(id+"F0.wireOp",EDGE,"E83.3.2.0"),sQuery(id+"F0.wireOp",EDGE,"E83.3.2.1"),sQuery(id+"F0.wireOp",EDGE,"E83.3.2.2"),sQuery(id+"F0.wireOp",EDGE,"E83.3.2.3"),sQuery(id+"F0.wireOp",EDGE,"E83.3.3.0"),sQuery(id+"F0.wireOp",EDGE,"E83.3.3.1"),sQuery(id+"F0.wireOp",EDGE,"E83.3.3.2"),sQuery(id+"F0.wireOp",EDGE,"E83.3.3.3"),sQuery(id+"F0.wireOp",EDGE,"E83.3.4.0"),sQuery(id+"F0.wireOp",EDGE,"E83.3.4.1"),sQuery(id+"F0.wireOp",EDGE,"E83.3.4.2"),sQuery(id+"F0.wireOp",EDGE,"E83.3.4.3"),sQuery(id+"F0.wireOp",EDGE,"E83.3.5.0"),sQuery(id+"F0.wireOp",EDGE,"E83.3.5.1"),sQuery(id+"F0.wireOp",EDGE,"E83.3.5.2"),sQuery(id+"F0.wireOp",EDGE,"E83.3.5.3"),sQuery(id+"F0.wireOp",EDGE,"E84.bottom"),sQuery(id+"F0.wireOp",EDGE,"E84.top"),sQuery(id+"F0.wireOp",EDGE,"E84.left"),sQuery(id+"F0.wireOp",EDGE,"E84.right"),sQuery(id+"F0.wireOp",EDGE,"E85.bottom"),sQuery(id+"F0.wireOp",EDGE,"E85.top"),sQuery(id+"F0.wireOp",EDGE,"E85.left"),sQuery(id+"F0.wireOp",EDGE,"E85.right"),sQuery(id+"F0.wireOp",EDGE,"E86.bottom"),sQuery(id+"F0.wireOp",EDGE,"E86.top"),sQuery(id+"F0.wireOp",EDGE,"E86.left"),sQuery(id+"F0.wireOp",EDGE,"E86.right"),sQuery(id+"F0.wireOp",EDGE,"E87.bottom"),sQuery(id+"F0.wireOp",EDGE,"E87.top"),sQuery(id+"F0.wireOp",EDGE,"E87.left"),sQuery(id+"F0.wireOp",EDGE,"E87.right"),sQuery(id+"F0.wireOp",EDGE,"E88.bottom"),sQuery(id+"F0.wireOp",EDGE,"E88.left"),sQuery(id+"F0.wireOp",EDGE,"E88.right"),sQuery(id+"F0.wireOp",EDGE,"E89.bottom"),sQuery(id+"F0.wireOp",EDGE,"E89.left"),sQuery(id+"F0.wireOp",EDGE,"E89.right"),sQuery(id+"F0.wireOp",EDGE,"E91.MirrorCS"),sQuery(id+"F0.wireOp",EDGE,"E92.MirrorCS"),sQuery(id+"F0.wireOp",EDGE,"E93.MirrorCS")])]});
            var Q1;
            Q1=makeQuery(id+"F4.opExtrude","SWEPT_BODY",BODY,{"disambiguationData":[OSD([sQuery(id+"F3.wireOp",EDGE,"E95.top"),sQuery(id+"F3.wireOp",EDGE,"E95.left"),sQuery(id+"F3.wireOp",EDGE,"E95.right"),sQuery(id+"F3.wireOp",EDGE,"E96.top"),sQuery(id+"F3.wireOp",EDGE,"E96.left"),sQuery(id+"F3.wireOp",EDGE,"E96.right")])]});
            var Q2;
            Q2=makeQuery(id+"F5.opExtrude","SWEPT_BODY",BODY,{"disambiguationData":[OSD([sQuery(id+"F0.wireOp",EDGE,"E1.bottom"),sQuery(id+"F0.wireOp",EDGE,"E1.top"),sQuery(id+"F0.wireOp",EDGE,"E1.left"),sQuery(id+"F0.wireOp",EDGE,"E1.right"),sQuery(id+"F0.wireOp",EDGE,"E88.top"),sQuery(id+"F0.wireOp",EDGE,"E89.top"),sQuery(id+"F0.wireOp",EDGE,"E90.MirrorCS")])]});
            var Q3;
            Q3=makeQuery(id+"F7.opExtrude","SWEPT_BODY",BODY,{"disambiguationData":[OSD([sQuery(id+"F6.wireOp",EDGE,"E97"),sQuery(id+"F6.wireOp",EDGE,"E98"),sQuery(id+"F6.wireOp",EDGE,"E99"),sQuery(id+"F6.wireOp",EDGE,"E100"),sQuery(id+"F6.wireOp",EDGE,"E101"),sQuery(id+"F6.wireOp",EDGE,"E102"),sQuery(id+"F6.wireOp",EDGE,"E103"),sQuery(id+"F6.wireOp",EDGE,"E104"),sQuery(id+"F6.wireOp",EDGE,"E105"),sQuery(id+"F6.wireOp",EDGE,"E106")])]});
            var Q4;
            Q4=qCreatedBy(makeId("Origin.pointOp"),VERTEX);
            transform(context, id + "F8", {"entities" : qUnion([Q0, Q1, Q2, Q3]), "transformType" : TransformType.SCALE_UNIFORMLY, "scale" : 1 / 100, "makeCopy" : false, "scalePoint" : qUnion([Q4])});
        }
    });
